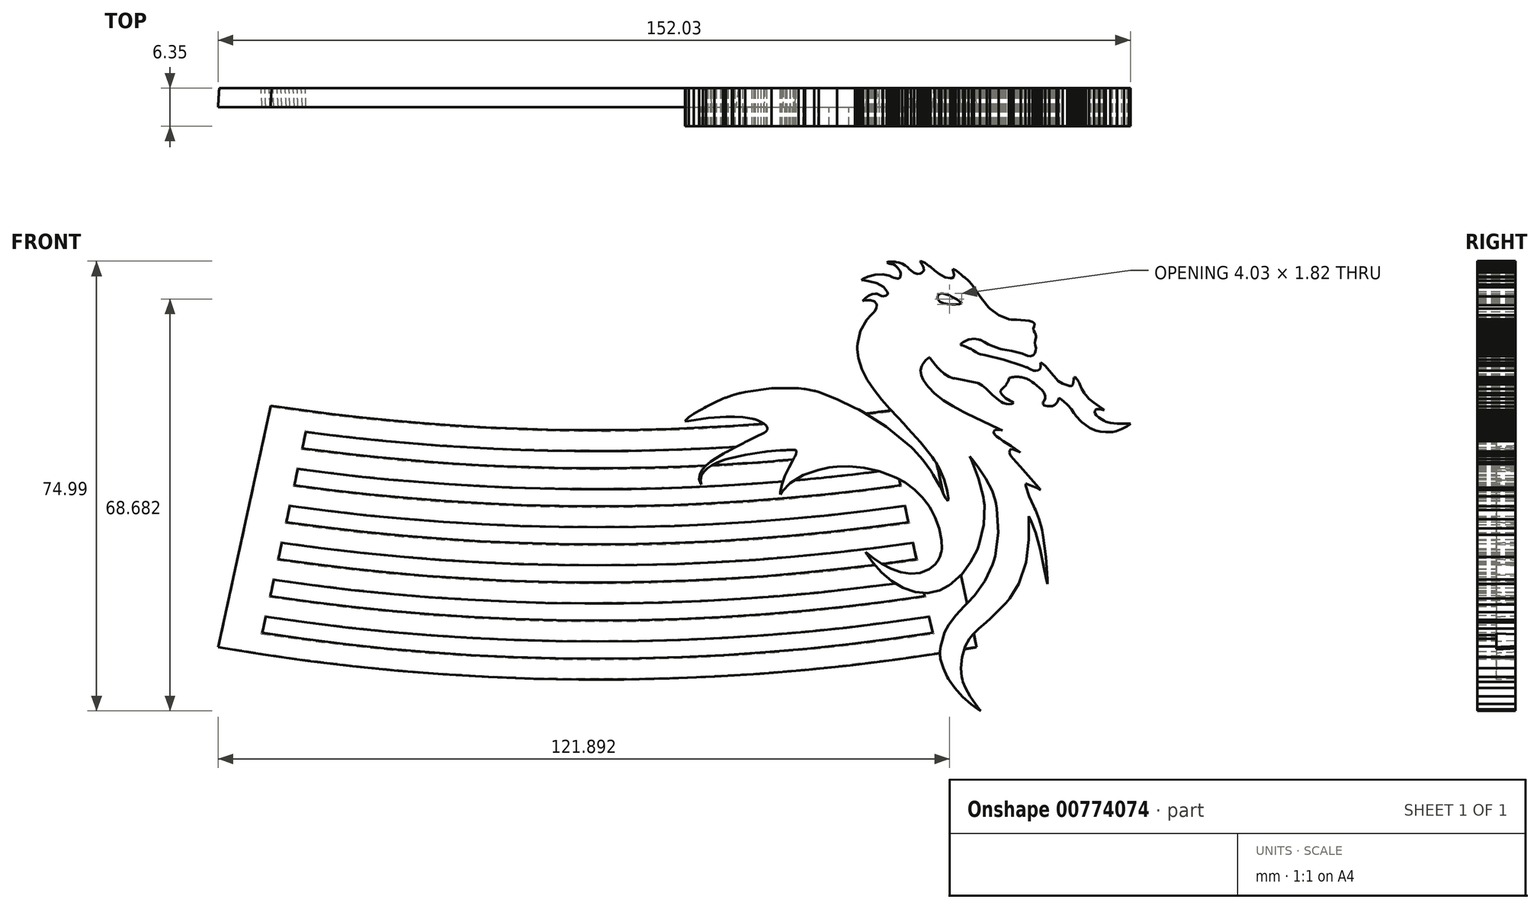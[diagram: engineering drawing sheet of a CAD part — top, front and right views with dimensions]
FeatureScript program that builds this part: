
annotation { "Feature Type Name" : "Feature", "Feature Type Description" : "" }
export const myFeature = defineFeature(function(context is Context, id is Id, definition is map)
    precondition{}
    {
        {
            var Q0;
            Q0=qCreatedBy(makeId("Front.planeOp"),FACE);
            var sketch = newSketch(context, id + "F0", { "sketchPlane" : qUnion([Q0])});
            skArc(sketch, "E0", {"start": v(-54.3, 4.59) * mm, "mid": v(0, 0.52) * mm, "end": v(54.3, 4.59) * mm});
            skArc(sketch, "E1", {"start": v(-48.68, 0.55) * mm, "mid": v(0, -2.65) * mm, "end": v(48.68, 0.55) * mm});
            skArc(sketch, "E2", {"start": v(-49.34, -2.48) * mm, "mid": v(0, -5.83) * mm, "end": v(49.34, -2.48) * mm});
            skArc(sketch, "E3", {"start": v(-50.03, -5.62) * mm, "mid": v(0, -9) * mm, "end": v(50.03, -5.62) * mm});
            skArc(sketch, "E4", {"start": v(-50.68, -8.64) * mm, "mid": v(0, -12.18) * mm, "end": v(50.68, -8.64) * mm});
            skArc(sketch, "E5", {"start": v(-51.37, -11.78) * mm, "mid": v(0, -15.35) * mm, "end": v(51.37, -11.78) * mm});
            skArc(sketch, "E6", {"start": v(-52.03, -14.8) * mm, "mid": v(0, -18.53) * mm, "end": v(52.03, -14.8) * mm});
            skArc(sketch, "E7", {"start": v(-52.71, -17.94) * mm, "mid": v(0, -21.7) * mm, "end": v(52.71, -17.94) * mm});
            skArc(sketch, "E8", {"start": v(-53.37, -20.95) * mm, "mid": v(0, -24.88) * mm, "end": v(53.37, -20.95) * mm});
            skArc(sketch, "E9", {"start": v(-54.05, -24.1) * mm, "mid": v(0, -28.05) * mm, "end": v(54.05, -24.1) * mm});
            skArc(sketch, "E10", {"start": v(-54.7, -27.1) * mm, "mid": v(0, -31.23) * mm, "end": v(54.7, -27.1) * mm});
            skArc(sketch, "E11", {"start": v(-55.4, -30.25) * mm, "mid": v(0, -34.4) * mm, "end": v(55.4, -30.25) * mm});
            skArc(sketch, "E12", {"start": v(-56.05, -33.25) * mm, "mid": v(0, -37.58) * mm, "end": v(56.05, -33.25) * mm});
            skArc(sketch, "E13", {"start": v(-63, -35.37) * mm, "mid": v(0, -40.75) * mm, "end": v(63, -35.37) * mm});
            skLineSegment(sketch, "E14", {"start": v(56.05, -33.25) * mm, "end": v(55.4, -30.25) * mm});
            skLineSegment(sketch, "E15", {"start": v(-56.05, -33.25) * mm, "end": v(-55.4, -30.25) * mm});
            skLineSegment(sketch, "E16", {"start": v(63, -35.37) * mm, "end": v(54.3, 4.59) * mm});
            skLineSegment(sketch, "E17", {"start": v(-63, -35.37) * mm, "end": v(-54.3, 4.59) * mm});
            skLineSegment(sketch, "E18.trimOffspring", {"start": v(49.34, -2.48) * mm, "end": v(48.68, 0.55) * mm});
            skLineSegment(sketch, "E19.trimOffspring", {"start": v(50.68, -8.64) * mm, "end": v(50.03, -5.62) * mm});
            skLineSegment(sketch, "E20.trimOffspring", {"start": v(52.03, -14.8) * mm, "end": v(51.37, -11.78) * mm});
            skLineSegment(sketch, "E21.trimOffspring", {"start": v(53.37, -20.95) * mm, "end": v(52.71, -17.94) * mm});
            skLineSegment(sketch, "E22.trimOffspring", {"start": v(54.7, -27.1) * mm, "end": v(54.05, -24.1) * mm});
            skLineSegment(sketch, "E23.trimOffspring", {"start": v(-49.34, -2.48) * mm, "end": v(-48.68, 0.55) * mm});
            skLineSegment(sketch, "E24.trimOffspring", {"start": v(-50.68, -8.64) * mm, "end": v(-50.03, -5.62) * mm});
            skLineSegment(sketch, "E25.trimOffspring", {"start": v(-52.03, -14.8) * mm, "end": v(-51.37, -11.78) * mm});
            skLineSegment(sketch, "E26.trimOffspring", {"start": v(-53.37, -20.95) * mm, "end": v(-52.71, -17.94) * mm});
            skLineSegment(sketch, "E27.trimOffspring", {"start": v(-54.7, -27.1) * mm, "end": v(-54.05, -24.1) * mm});
            skSolve(sketch);
        }
        {
            var Q0;
            Q0 = qSketchRegion(id + "F0", true);
            extrude(context, id + "F1", {"entities" : qUnion([Q0]), "depth" : 3.17 * mm, "offsetDistance" : 25.4 * mm, "hasDraft" : true, "draftAngle" : 3 * degree});
        }
        {
            var Q0;
            Q0=qCreatedBy(makeId("Front.planeOp"),FACE);
            var sketch = newSketch(context, id + "F2", { "sketchPlane" : qUnion([Q0])});
            skLineSegment(sketch, "E28", {"start": v(68.67, 9.41) * mm, "end": v(68.42, 8.83) * mm});
            skLineSegment(sketch, "E29", {"start": v(68.42, 8.83) * mm, "end": v(68.1, 8.27) * mm});
            skLineSegment(sketch, "E30", {"start": v(68.1, 8.27) * mm, "end": v(68.04, 8.16) * mm});
            skLineSegment(sketch, "E31", {"start": v(68.04, 8.16) * mm, "end": v(68, 8.1) * mm});
            skLineSegment(sketch, "E32", {"start": v(68, 8.1) * mm, "end": v(67.83, 7.9) * mm});
            skLineSegment(sketch, "E33", {"start": v(67.83, 7.9) * mm, "end": v(67.56, 7.67) * mm});
            skLineSegment(sketch, "E34", {"start": v(67.56, 7.67) * mm, "end": v(67.32, 7.43) * mm});
            skLineSegment(sketch, "E35", {"start": v(67.32, 7.43) * mm, "end": v(67.2, 7.21) * mm});
            skLineSegment(sketch, "E36", {"start": v(67.2, 7.21) * mm, "end": v(67.2, 7.14) * mm});
            skLineSegment(sketch, "E37", {"start": v(67.2, 7.14) * mm, "end": v(67.18, 7) * mm});
            skLineSegment(sketch, "E38", {"start": v(67.18, 7) * mm, "end": v(67.42, 6.57) * mm});
            skLineSegment(sketch, "E39", {"start": v(67.42, 6.57) * mm, "end": v(68.03, 6.05) * mm});
            skLineSegment(sketch, "E40", {"start": v(68.03, 6.05) * mm, "end": v(68.75, 5.6) * mm});
            skLineSegment(sketch, "E41", {"start": v(68.75, 5.6) * mm, "end": v(69.19, 5.37) * mm});
            skLineSegment(sketch, "E42", {"start": v(69.19, 5.37) * mm, "end": v(69.32, 5.29) * mm});
            skLineSegment(sketch, "E43", {"start": v(69.32, 5.29) * mm, "end": v(69.28, 5.21) * mm});
            skLineSegment(sketch, "E44", {"start": v(69.28, 5.21) * mm, "end": v(69.03, 5.06) * mm});
            skLineSegment(sketch, "E45", {"start": v(69.03, 5.06) * mm, "end": v(68.6, 5.02) * mm});
            skLineSegment(sketch, "E46", {"start": v(68.6, 5.02) * mm, "end": v(68.14, 5.07) * mm});
            skLineSegment(sketch, "E47", {"start": v(68.14, 5.07) * mm, "end": v(67.85, 5.14) * mm});
            skLineSegment(sketch, "E48", {"start": v(67.85, 5.14) * mm, "end": v(67.76, 5.17) * mm});
            skLineSegment(sketch, "E49", {"start": v(67.76, 5.17) * mm, "end": v(67.64, 5.2) * mm});
            skLineSegment(sketch, "E50", {"start": v(67.64, 5.2) * mm, "end": v(67.32, 5.38) * mm});
            skLineSegment(sketch, "E51", {"start": v(67.32, 5.38) * mm, "end": v(66.88, 5.7) * mm});
            skLineSegment(sketch, "E52", {"start": v(66.88, 5.7) * mm, "end": v(66.46, 6.05) * mm});
            skLineSegment(sketch, "E53", {"start": v(66.46, 6.05) * mm, "end": v(66.18, 6.3) * mm});
            skLineSegment(sketch, "E54", {"start": v(66.18, 6.3) * mm, "end": v(66.08, 6.37) * mm});
            skLineSegment(sketch, "E55", {"start": v(66.08, 6.37) * mm, "end": v(65.9, 6.5) * mm});
            skLineSegment(sketch, "E56", {"start": v(65.9, 6.5) * mm, "end": v(65.42, 6.96) * mm});
            skLineSegment(sketch, "E57", {"start": v(65.42, 6.96) * mm, "end": v(64.8, 7.59) * mm});
            skLineSegment(sketch, "E58", {"start": v(64.8, 7.59) * mm, "end": v(64.12, 8.14) * mm});
            skLineSegment(sketch, "E59", {"start": v(64.12, 8.14) * mm, "end": v(63.52, 8.48) * mm});
            skLineSegment(sketch, "E60", {"start": v(63.52, 8.48) * mm, "end": v(63.3, 8.54) * mm});
            skLineSegment(sketch, "E61", {"start": v(63.3, 8.54) * mm, "end": v(63, 8.64) * mm});
            skLineSegment(sketch, "E62", {"start": v(63, 8.64) * mm, "end": v(59.85, 9.26) * mm});
            skLineSegment(sketch, "E63", {"start": v(59.85, 9.26) * mm, "end": v(59.53, 9.3) * mm});
            skLineSegment(sketch, "E64", {"start": v(59.53, 9.3) * mm, "end": v(59.3, 9.34) * mm});
            skLineSegment(sketch, "E65", {"start": v(59.3, 9.34) * mm, "end": v(58.62, 9.58) * mm});
            skLineSegment(sketch, "E66", {"start": v(58.62, 9.58) * mm, "end": v(57.8, 10.08) * mm});
            skLineSegment(sketch, "E67", {"start": v(57.8, 10.08) * mm, "end": v(57.09, 10.72) * mm});
            skLineSegment(sketch, "E68", {"start": v(57.09, 10.72) * mm, "end": v(56.6, 11.24) * mm});
            skLineSegment(sketch, "E69", {"start": v(56.6, 11.24) * mm, "end": v(56.45, 11.42) * mm});
            skLineSegment(sketch, "E70", {"start": v(56.45, 11.42) * mm, "end": v(56.35, 11.53) * mm});
            skLineSegment(sketch, "E71", {"start": v(56.35, 11.53) * mm, "end": v(55.43, 12.69) * mm});
            skLineSegment(sketch, "E72", {"start": v(55.43, 12.69) * mm, "end": v(55.34, 12.8) * mm});
            skLineSegment(sketch, "E73", {"start": v(55.34, 12.8) * mm, "end": v(55.33, 12.82) * mm});
            skLineSegment(sketch, "E74", {"start": v(55.33, 12.82) * mm, "end": v(55.1, 12.72) * mm});
            skLineSegment(sketch, "E75", {"start": v(55.1, 12.72) * mm, "end": v(54.7, 12.3) * mm});
            skLineSegment(sketch, "E76", {"start": v(54.7, 12.3) * mm, "end": v(54.32, 11.84) * mm});
            skLineSegment(sketch, "E77", {"start": v(54.32, 11.84) * mm, "end": v(54.15, 11.6) * mm});
            skLineSegment(sketch, "E78", {"start": v(54.15, 11.6) * mm, "end": v(54.13, 11.56) * mm});
            skLineSegment(sketch, "E79", {"start": v(54.13, 11.56) * mm, "end": v(54.03, 11.35) * mm});
            skLineSegment(sketch, "E80", {"start": v(54.03, 11.35) * mm, "end": v(53.86, 10.65) * mm});
            skLineSegment(sketch, "E81", {"start": v(53.86, 10.65) * mm, "end": v(53.95, 9.83) * mm});
            skLineSegment(sketch, "E82", {"start": v(53.95, 9.83) * mm, "end": v(54.31, 9.06) * mm});
            skLineSegment(sketch, "E83", {"start": v(54.31, 9.06) * mm, "end": v(54.72, 8.46) * mm});
            skLineSegment(sketch, "E84", {"start": v(54.72, 8.46) * mm, "end": v(54.86, 8.27) * mm});
            skLineSegment(sketch, "E85", {"start": v(54.86, 8.27) * mm, "end": v(55.16, 7.88) * mm});
            skLineSegment(sketch, "E86", {"start": v(55.16, 7.88) * mm, "end": v(56.17, 6.81) * mm});
            skLineSegment(sketch, "E87", {"start": v(56.17, 6.81) * mm, "end": v(57.62, 5.65) * mm});
            skLineSegment(sketch, "E88", {"start": v(57.62, 5.65) * mm, "end": v(59.21, 4.66) * mm});
            skLineSegment(sketch, "E89", {"start": v(59.21, 4.66) * mm, "end": v(60.51, 3.98) * mm});
            skLineSegment(sketch, "E90", {"start": v(60.51, 3.98) * mm, "end": v(60.95, 3.76) * mm});
            skLineSegment(sketch, "E91", {"start": v(60.95, 3.76) * mm, "end": v(61.49, 3.49) * mm});
            skLineSegment(sketch, "E92", {"start": v(61.49, 3.49) * mm, "end": v(66.94, 0.9) * mm});
            skLineSegment(sketch, "E93", {"start": v(66.94, 0.9) * mm, "end": v(67.5, 0.66) * mm});
            skLineSegment(sketch, "E94", {"start": v(67.5, 0.66) * mm, "end": v(67.4, 0.69) * mm});
            skLineSegment(sketch, "E95", {"start": v(67.4, 0.69) * mm, "end": v(67.09, 0.75) * mm});
            skLineSegment(sketch, "E96", {"start": v(67.09, 0.75) * mm, "end": v(66.64, 0.78) * mm});
            skLineSegment(sketch, "E97", {"start": v(66.64, 0.78) * mm, "end": v(66.25, 0.68) * mm});
            skLineSegment(sketch, "E98", {"start": v(66.25, 0.68) * mm, "end": v(66.06, 0.47) * mm});
            skLineSegment(sketch, "E99", {"start": v(66.06, 0.47) * mm, "end": v(66.04, 0.39) * mm});
            skLineSegment(sketch, "E100", {"start": v(66.04, 0.39) * mm, "end": v(66.03, 0.3) * mm});
            skLineSegment(sketch, "E101", {"start": v(66.03, 0.3) * mm, "end": v(66.17, 0.01) * mm});
            skLineSegment(sketch, "E102", {"start": v(66.17, 0.01) * mm, "end": v(66.56, -0.37) * mm});
            skLineSegment(sketch, "E103", {"start": v(66.56, -0.37) * mm, "end": v(67.03, -0.71) * mm});
            skLineSegment(sketch, "E104", {"start": v(67.03, -0.71) * mm, "end": v(67.3, -0.89) * mm});
            skLineSegment(sketch, "E105", {"start": v(67.3, -0.89) * mm, "end": v(67.37, -0.94) * mm});
            skLineSegment(sketch, "E106", {"start": v(67.37, -0.94) * mm, "end": v(67.63, -1.13) * mm});
            skLineSegment(sketch, "E107", {"start": v(67.63, -1.13) * mm, "end": v(68.94, -2) * mm});
            skLineSegment(sketch, "E108", {"start": v(68.94, -2) * mm, "end": v(70.25, -2.86) * mm});
            skLineSegment(sketch, "E109", {"start": v(70.25, -2.86) * mm, "end": v(70.5, -3.05) * mm});
            skLineSegment(sketch, "E110", {"start": v(70.5, -3.05) * mm, "end": v(70.45, -3.02) * mm});
            skLineSegment(sketch, "E111", {"start": v(70.45, -3.02) * mm, "end": v(70.28, -2.94) * mm});
            skLineSegment(sketch, "E112", {"start": v(70.28, -2.94) * mm, "end": v(69.99, -2.8) * mm});
            skLineSegment(sketch, "E113", {"start": v(69.99, -2.8) * mm, "end": v(69.66, -2.66) * mm});
            skLineSegment(sketch, "E114", {"start": v(69.66, -2.66) * mm, "end": v(69.33, -2.55) * mm});
            skLineSegment(sketch, "E115", {"start": v(69.33, -2.55) * mm, "end": v(69.04, -2.5) * mm});
            skLineSegment(sketch, "E116", {"start": v(69.04, -2.5) * mm, "end": v(68.8, -2.55) * mm});
            skLineSegment(sketch, "E117", {"start": v(68.8, -2.55) * mm, "end": v(68.68, -2.74) * mm});
            skLineSegment(sketch, "E118", {"start": v(68.68, -2.74) * mm, "end": v(68.67, -3) * mm});
            skLineSegment(sketch, "E119", {"start": v(68.67, -3) * mm, "end": v(68.68, -3.09) * mm});
            skLineSegment(sketch, "E120", {"start": v(68.68, -3.09) * mm, "end": v(68.7, -3.23) * mm});
            skLineSegment(sketch, "E121", {"start": v(68.7, -3.23) * mm, "end": v(68.9, -3.62) * mm});
            skLineSegment(sketch, "E122", {"start": v(68.9, -3.62) * mm, "end": v(69.3, -4.14) * mm});
            skLineSegment(sketch, "E123", {"start": v(69.3, -4.14) * mm, "end": v(69.77, -4.64) * mm});
            skLineSegment(sketch, "E124", {"start": v(69.77, -4.64) * mm, "end": v(70.08, -4.96) * mm});
            skLineSegment(sketch, "E125", {"start": v(70.08, -4.96) * mm, "end": v(70.18, -5.08) * mm});
            skLineSegment(sketch, "E126", {"start": v(70.18, -5.08) * mm, "end": v(70.49, -5.43) * mm});
            skLineSegment(sketch, "E127", {"start": v(70.49, -5.43) * mm, "end": v(73.52, -8.92) * mm});
            skLineSegment(sketch, "E128", {"start": v(73.52, -8.92) * mm, "end": v(73.83, -9.27) * mm});
            skLineSegment(sketch, "E129", {"start": v(73.83, -9.27) * mm, "end": v(73.7, -9.2) * mm});
            skLineSegment(sketch, "E130", {"start": v(73.7, -9.2) * mm, "end": v(73.27, -8.98) * mm});
            skLineSegment(sketch, "E131", {"start": v(73.27, -8.98) * mm, "end": v(72.63, -8.69) * mm});
            skLineSegment(sketch, "E132", {"start": v(72.63, -8.69) * mm, "end": v(71.97, -8.43) * mm});
            skLineSegment(sketch, "E133", {"start": v(71.97, -8.43) * mm, "end": v(71.53, -8.29) * mm});
            skLineSegment(sketch, "E134", {"start": v(71.53, -8.29) * mm, "end": v(71.37, -8.25) * mm});
            skLineSegment(sketch, "E135", {"start": v(71.37, -8.25) * mm, "end": v(71.4, -8.6) * mm});
            skLineSegment(sketch, "E136", {"start": v(71.4, -8.6) * mm, "end": v(71.94, -10.34) * mm});
            skLineSegment(sketch, "E137", {"start": v(71.94, -10.34) * mm, "end": v(72.72, -12.01) * mm});
            skLineSegment(sketch, "E138", {"start": v(72.72, -12.01) * mm, "end": v(72.86, -12.33) * mm});
            skLineSegment(sketch, "E139", {"start": v(72.86, -12.33) * mm, "end": v(73, -12.62) * mm});
            skLineSegment(sketch, "E140", {"start": v(73, -12.62) * mm, "end": v(73.58, -14.14) * mm});
            skLineSegment(sketch, "E141", {"start": v(73.58, -14.14) * mm, "end": v(74.02, -15.71) * mm});
            skLineSegment(sketch, "E142", {"start": v(74.02, -15.71) * mm, "end": v(74.08, -16.03) * mm});
            skLineSegment(sketch, "E143", {"start": v(74.08, -16.03) * mm, "end": v(74.2, -16.77) * mm});
            skLineSegment(sketch, "E144", {"start": v(74.2, -16.77) * mm, "end": v(74.7, -20.47) * mm});
            skLineSegment(sketch, "E145", {"start": v(74.7, -20.47) * mm, "end": v(74.97, -24.2) * mm});
            skLineSegment(sketch, "E146", {"start": v(74.97, -24.2) * mm, "end": v(75, -24.95) * mm});
            skLineSegment(sketch, "E147", {"start": v(75, -24.95) * mm, "end": v(74.82, -24.23) * mm});
            skLineSegment(sketch, "E148", {"start": v(74.82, -24.23) * mm, "end": v(74.38, -22.06) * mm});
            skLineSegment(sketch, "E149", {"start": v(74.38, -22.06) * mm, "end": v(73.79, -19.2) * mm});
            skLineSegment(sketch, "E150", {"start": v(73.79, -19.2) * mm, "end": v(73.01, -16.38) * mm});
            skLineSegment(sketch, "E151", {"start": v(73.01, -16.38) * mm, "end": v(72.2, -14.31) * mm});
            skLineSegment(sketch, "E152", {"start": v(72.2, -14.31) * mm, "end": v(71.87, -13.66) * mm});
            skLineSegment(sketch, "E153", {"start": v(71.87, -13.66) * mm, "end": v(71.9, -14.63) * mm});
            skLineSegment(sketch, "E154", {"start": v(71.9, -14.63) * mm, "end": v(71.87, -17.54) * mm});
            skLineSegment(sketch, "E155", {"start": v(71.87, -17.54) * mm, "end": v(71.4, -21.31) * mm});
            skLineSegment(sketch, "E156", {"start": v(71.4, -21.31) * mm, "end": v(70.21, -24.88) * mm});
            skLineSegment(sketch, "E157", {"start": v(70.21, -24.88) * mm, "end": v(68.7, -27.4) * mm});
            skLineSegment(sketch, "E158", {"start": v(68.7, -27.4) * mm, "end": v(68.05, -28.11) * mm});
            skLineSegment(sketch, "E159", {"start": v(68.05, -28.11) * mm, "end": v(67.8, -28.38) * mm});
            skLineSegment(sketch, "E160", {"start": v(67.8, -28.38) * mm, "end": v(66.57, -29.67) * mm});
            skLineSegment(sketch, "E161", {"start": v(66.57, -29.67) * mm, "end": v(65.27, -30.9) * mm});
            skLineSegment(sketch, "E162", {"start": v(65.27, -30.9) * mm, "end": v(65, -31.15) * mm});
            skLineSegment(sketch, "E163", {"start": v(65, -31.15) * mm, "end": v(64.76, -31.36) * mm});
            skLineSegment(sketch, "E164", {"start": v(64.76, -31.36) * mm, "end": v(63.57, -32.36) * mm});
            skLineSegment(sketch, "E165", {"start": v(63.57, -32.36) * mm, "end": v(62.48, -33.46) * mm});
            skLineSegment(sketch, "E166", {"start": v(62.48, -33.46) * mm, "end": v(62.29, -33.72) * mm});
            skLineSegment(sketch, "E167", {"start": v(62.29, -33.72) * mm, "end": v(62, -34.11) * mm});
            skLineSegment(sketch, "E168", {"start": v(62, -34.11) * mm, "end": v(61.3, -35.4) * mm});
            skLineSegment(sketch, "E169", {"start": v(61.3, -35.4) * mm, "end": v(60.74, -37.16) * mm});
            skLineSegment(sketch, "E170", {"start": v(60.74, -37.16) * mm, "end": v(60.6, -39) * mm});
            skLineSegment(sketch, "E171", {"start": v(60.6, -39) * mm, "end": v(60.72, -40.45) * mm});
            skLineSegment(sketch, "E172", {"start": v(60.72, -40.45) * mm, "end": v(60.82, -40.92) * mm});
            skLineSegment(sketch, "E173", {"start": v(60.82, -40.92) * mm, "end": v(60.9, -41.28) * mm});
            skLineSegment(sketch, "E174", {"start": v(60.9, -41.28) * mm, "end": v(61.3, -42.32) * mm});
            skLineSegment(sketch, "E175", {"start": v(61.3, -42.32) * mm, "end": v(62.07, -43.66) * mm});
            skLineSegment(sketch, "E176", {"start": v(62.07, -43.66) * mm, "end": v(62.96, -44.94) * mm});
            skLineSegment(sketch, "E177", {"start": v(62.96, -44.94) * mm, "end": v(63.63, -45.83) * mm});
            skLineSegment(sketch, "E178", {"start": v(63.63, -45.83) * mm, "end": v(63.85, -46.13) * mm});
            skLineSegment(sketch, "E179", {"start": v(63.85, -46.13) * mm, "end": v(63.45, -45.87) * mm});
            skLineSegment(sketch, "E180", {"start": v(63.45, -45.87) * mm, "end": v(62.31, -45.02) * mm});
            skLineSegment(sketch, "E181", {"start": v(62.31, -45.02) * mm, "end": v(60.86, -43.74) * mm});
            skLineSegment(sketch, "E182", {"start": v(60.86, -43.74) * mm, "end": v(59.55, -42.31) * mm});
            skLineSegment(sketch, "E183", {"start": v(59.55, -42.31) * mm, "end": v(58.72, -41.17) * mm});
            skLineSegment(sketch, "E184", {"start": v(58.72, -41.17) * mm, "end": v(58.48, -40.76) * mm});
            skLineSegment(sketch, "E185", {"start": v(58.48, -40.76) * mm, "end": v(58.32, -40.48) * mm});
            skLineSegment(sketch, "E186", {"start": v(58.32, -40.48) * mm, "end": v(57.63, -39.02) * mm});
            skLineSegment(sketch, "E187", {"start": v(57.63, -39.02) * mm, "end": v(57.18, -37.47) * mm});
            skLineSegment(sketch, "E188", {"start": v(57.18, -37.47) * mm, "end": v(57.14, -37.16) * mm});
            skLineSegment(sketch, "E189", {"start": v(57.14, -37.16) * mm, "end": v(57.1, -36.92) * mm});
            skLineSegment(sketch, "E190", {"start": v(57.1, -36.92) * mm, "end": v(57.1, -36.21) * mm});
            skLineSegment(sketch, "E191", {"start": v(57.1, -36.21) * mm, "end": v(57.22, -35.3) * mm});
            skLineSegment(sketch, "E192", {"start": v(57.22, -35.3) * mm, "end": v(57.44, -34.4) * mm});
            skLineSegment(sketch, "E193", {"start": v(57.44, -34.4) * mm, "end": v(57.64, -33.71) * mm});
            skLineSegment(sketch, "E194", {"start": v(57.64, -33.71) * mm, "end": v(57.7, -33.49) * mm});
            skLineSegment(sketch, "E195", {"start": v(57.7, -33.49) * mm, "end": v(57.85, -33.03) * mm});
            skLineSegment(sketch, "E196", {"start": v(57.85, -33.03) * mm, "end": v(58.52, -31.74) * mm});
            skLineSegment(sketch, "E197", {"start": v(58.52, -31.74) * mm, "end": v(59.72, -30.17) * mm});
            skLineSegment(sketch, "E198", {"start": v(59.72, -30.17) * mm, "end": v(61.1, -28.71) * mm});
            skLineSegment(sketch, "E199", {"start": v(61.1, -28.71) * mm, "end": v(62.11, -27.67) * mm});
            skLineSegment(sketch, "E200", {"start": v(62.11, -27.67) * mm, "end": v(62.44, -27.31) * mm});
            skLineSegment(sketch, "E201", {"start": v(62.44, -27.31) * mm, "end": v(62.84, -26.87) * mm});
            skLineSegment(sketch, "E202", {"start": v(62.84, -26.87) * mm, "end": v(64.59, -24.42) * mm});
            skLineSegment(sketch, "E203", {"start": v(64.59, -24.42) * mm, "end": v(65.87, -21.72) * mm});
            skLineSegment(sketch, "E204", {"start": v(65.87, -21.72) * mm, "end": v(66.05, -21.15) * mm});
            skLineSegment(sketch, "E205", {"start": v(66.05, -21.15) * mm, "end": v(66.28, -20.35) * mm});
            skLineSegment(sketch, "E206", {"start": v(66.28, -20.35) * mm, "end": v(66.78, -16.38) * mm});
            skLineSegment(sketch, "E207", {"start": v(66.78, -16.38) * mm, "end": v(66.53, -12.38) * mm});
            skLineSegment(sketch, "E208", {"start": v(66.53, -12.38) * mm, "end": v(66.4, -11.57) * mm});
            skLineSegment(sketch, "E209", {"start": v(66.4, -11.57) * mm, "end": v(66.3, -11.02) * mm});
            skLineSegment(sketch, "E210", {"start": v(66.3, -11.02) * mm, "end": v(65.76, -9.4) * mm});
            skLineSegment(sketch, "E211", {"start": v(65.76, -9.4) * mm, "end": v(64.73, -7.37) * mm});
            skLineSegment(sketch, "E212", {"start": v(64.73, -7.37) * mm, "end": v(63.44, -5.47) * mm});
            skLineSegment(sketch, "E213", {"start": v(63.44, -5.47) * mm, "end": v(62.41, -4.14) * mm});
            skLineSegment(sketch, "E214", {"start": v(62.41, -4.14) * mm, "end": v(62.06, -3.71) * mm});
            skLineSegment(sketch, "E215", {"start": v(62.06, -3.71) * mm, "end": v(62.33, -4.33) * mm});
            skLineSegment(sketch, "E216", {"start": v(62.33, -4.33) * mm, "end": v(63.48, -7.34) * mm});
            skLineSegment(sketch, "E217", {"start": v(63.48, -7.34) * mm, "end": v(64.3, -10.46) * mm});
            skLineSegment(sketch, "E218", {"start": v(64.3, -10.46) * mm, "end": v(64.4, -11.13) * mm});
            skLineSegment(sketch, "E219", {"start": v(64.4, -11.13) * mm, "end": v(64.49, -11.79) * mm});
            skLineSegment(sketch, "E220", {"start": v(64.49, -11.79) * mm, "end": v(64.4, -15.05) * mm});
            skLineSegment(sketch, "E221", {"start": v(64.4, -15.05) * mm, "end": v(63.65, -18.22) * mm});
            skLineSegment(sketch, "E222", {"start": v(63.65, -18.22) * mm, "end": v(63.43, -18.84) * mm});
            skLineSegment(sketch, "E223", {"start": v(63.43, -18.84) * mm, "end": v(63.27, -19.27) * mm});
            skLineSegment(sketch, "E224", {"start": v(63.27, -19.27) * mm, "end": v(62.19, -21.37) * mm});
            skLineSegment(sketch, "E225", {"start": v(62.19, -21.37) * mm, "end": v(60.74, -23.3) * mm});
            skLineSegment(sketch, "E226", {"start": v(60.74, -23.3) * mm, "end": v(60.4, -23.65) * mm});
            skLineSegment(sketch, "E227", {"start": v(60.4, -23.65) * mm, "end": v(60.29, -23.76) * mm});
            skLineSegment(sketch, "E228", {"start": v(60.29, -23.76) * mm, "end": v(59.08, -24.8) * mm});
            skLineSegment(sketch, "E229", {"start": v(59.08, -24.8) * mm, "end": v(58.96, -24.89) * mm});
            skLineSegment(sketch, "E230", {"start": v(58.96, -24.89) * mm, "end": v(58.52, -25.24) * mm});
            skLineSegment(sketch, "E231", {"start": v(58.52, -25.24) * mm, "end": v(57, -26.03) * mm});
            skLineSegment(sketch, "E232", {"start": v(57, -26.03) * mm, "end": v(54.98, -26.47) * mm});
            skLineSegment(sketch, "E233", {"start": v(54.98, -26.47) * mm, "end": v(52.93, -26.29) * mm});
            skLineSegment(sketch, "E234", {"start": v(52.93, -26.29) * mm, "end": v(50.93, -25.6) * mm});
            skLineSegment(sketch, "E235", {"start": v(50.93, -25.6) * mm, "end": v(49.05, -24.48) * mm});
            skLineSegment(sketch, "E236", {"start": v(49.05, -24.48) * mm, "end": v(47.34, -23.05) * mm});
            skLineSegment(sketch, "E237", {"start": v(47.34, -23.05) * mm, "end": v(45.88, -21.39) * mm});
            skLineSegment(sketch, "E238", {"start": v(45.88, -21.39) * mm, "end": v(44.98, -20.06) * mm});
            skLineSegment(sketch, "E239", {"start": v(44.98, -20.06) * mm, "end": v(44.73, -19.6) * mm});
            skLineSegment(sketch, "E240", {"start": v(44.73, -19.6) * mm, "end": v(45.02, -19.87) * mm});
            skLineSegment(sketch, "E241", {"start": v(45.02, -19.87) * mm, "end": v(45.95, -20.63) * mm});
            skLineSegment(sketch, "E242", {"start": v(45.95, -20.63) * mm, "end": v(47.38, -21.6) * mm});
            skLineSegment(sketch, "E243", {"start": v(47.38, -21.6) * mm, "end": v(48.94, -22.42) * mm});
            skLineSegment(sketch, "E244", {"start": v(48.94, -22.42) * mm, "end": v(50.57, -23) * mm});
            skLineSegment(sketch, "E245", {"start": v(50.57, -23) * mm, "end": v(52.21, -23.26) * mm});
            skLineSegment(sketch, "E246", {"start": v(52.21, -23.26) * mm, "end": v(53.8, -23.12) * mm});
            skLineSegment(sketch, "E247", {"start": v(53.8, -23.12) * mm, "end": v(55.28, -22.5) * mm});
            skLineSegment(sketch, "E248", {"start": v(55.28, -22.5) * mm, "end": v(56.31, -21.65) * mm});
            skLineSegment(sketch, "E249", {"start": v(56.31, -21.65) * mm, "end": v(56.58, -21.3) * mm});
            skLineSegment(sketch, "E250", {"start": v(56.58, -21.3) * mm, "end": v(56.68, -21.16) * mm});
            skLineSegment(sketch, "E251", {"start": v(56.68, -21.16) * mm, "end": v(57.06, -20.4) * mm});
            skLineSegment(sketch, "E252", {"start": v(57.06, -20.4) * mm, "end": v(57.3, -19.67) * mm});
            skLineSegment(sketch, "E253", {"start": v(57.3, -19.67) * mm, "end": v(57.31, -19.54) * mm});
            skLineSegment(sketch, "E254", {"start": v(57.31, -19.54) * mm, "end": v(57.38, -19.07) * mm});
            skLineSegment(sketch, "E255", {"start": v(57.38, -19.07) * mm, "end": v(57.34, -17.64) * mm});
            skLineSegment(sketch, "E256", {"start": v(57.34, -17.64) * mm, "end": v(56.95, -15.7) * mm});
            skLineSegment(sketch, "E257", {"start": v(56.95, -15.7) * mm, "end": v(56.25, -13.83) * mm});
            skLineSegment(sketch, "E258", {"start": v(56.25, -13.83) * mm, "end": v(55.6, -12.56) * mm});
            skLineSegment(sketch, "E259", {"start": v(55.6, -12.56) * mm, "end": v(55.35, -12.15) * mm});
            skLineSegment(sketch, "E260", {"start": v(55.35, -12.15) * mm, "end": v(55.09, -11.74) * mm});
            skLineSegment(sketch, "E261", {"start": v(55.09, -11.74) * mm, "end": v(54.2, -10.58) * mm});
            skLineSegment(sketch, "E262", {"start": v(54.2, -10.58) * mm, "end": v(52.8, -9.19) * mm});
            skLineSegment(sketch, "E263", {"start": v(52.8, -9.19) * mm, "end": v(51.22, -8.02) * mm});
            skLineSegment(sketch, "E264", {"start": v(51.22, -8.02) * mm, "end": v(49.92, -7.3) * mm});
            skLineSegment(sketch, "E265", {"start": v(49.92, -7.3) * mm, "end": v(49.47, -7.11) * mm});
            skLineSegment(sketch, "E266", {"start": v(49.47, -7.11) * mm, "end": v(48.85, -6.85) * mm});
            skLineSegment(sketch, "E267", {"start": v(48.85, -6.85) * mm, "end": v(46.96, -6.19) * mm});
            skLineSegment(sketch, "E268", {"start": v(46.96, -6.19) * mm, "end": v(44.46, -5.59) * mm});
            skLineSegment(sketch, "E269", {"start": v(44.46, -5.59) * mm, "end": v(41.92, -5.34) * mm});
            skLineSegment(sketch, "E270", {"start": v(41.92, -5.34) * mm, "end": v(39.9, -5.4) * mm});
            skLineSegment(sketch, "E271", {"start": v(39.9, -5.4) * mm, "end": v(39.24, -5.47) * mm});
            skLineSegment(sketch, "E272", {"start": v(39.24, -5.47) * mm, "end": v(38.61, -5.55) * mm});
            skLineSegment(sketch, "E273", {"start": v(38.61, -5.55) * mm, "end": v(36.74, -5.94) * mm});
            skLineSegment(sketch, "E274", {"start": v(36.74, -5.94) * mm, "end": v(34.31, -6.81) * mm});
            skLineSegment(sketch, "E275", {"start": v(34.31, -6.81) * mm, "end": v(32.16, -8.15) * mm});
            skLineSegment(sketch, "E276", {"start": v(32.16, -8.15) * mm, "end": v(30.8, -9.52) * mm});
            skLineSegment(sketch, "E277", {"start": v(30.8, -9.52) * mm, "end": v(30.46, -10.05) * mm});
            skLineSegment(sketch, "E278", {"start": v(30.46, -10.05) * mm, "end": v(30.48, -9.64) * mm});
            skLineSegment(sketch, "E279", {"start": v(30.48, -9.64) * mm, "end": v(30.73, -8.42) * mm});
            skLineSegment(sketch, "E280", {"start": v(30.73, -8.42) * mm, "end": v(31.26, -6.95) * mm});
            skLineSegment(sketch, "E281", {"start": v(31.26, -6.95) * mm, "end": v(31.96, -5.52) * mm});
            skLineSegment(sketch, "E282", {"start": v(31.96, -5.52) * mm, "end": v(32.52, -4.42) * mm});
            skLineSegment(sketch, "E283", {"start": v(32.52, -4.42) * mm, "end": v(32.7, -4.05) * mm});
            skLineSegment(sketch, "E284", {"start": v(32.7, -4.05) * mm, "end": v(32.74, -3.97) * mm});
            skLineSegment(sketch, "E285", {"start": v(32.74, -3.97) * mm, "end": v(32.87, -3.74) * mm});
            skLineSegment(sketch, "E286", {"start": v(32.87, -3.74) * mm, "end": v(33.06, -3.35) * mm});
            skLineSegment(sketch, "E287", {"start": v(33.06, -3.35) * mm, "end": v(33.17, -2.96) * mm});
            skLineSegment(sketch, "E288", {"start": v(33.17, -2.96) * mm, "end": v(33.12, -2.71) * mm});
            skLineSegment(sketch, "E289", {"start": v(33.12, -2.71) * mm, "end": v(33.07, -2.67) * mm});
            skLineSegment(sketch, "E290", {"start": v(33.07, -2.67) * mm, "end": v(33.01, -2.62) * mm});
            skLineSegment(sketch, "E291", {"start": v(33.01, -2.62) * mm, "end": v(32.74, -2.59) * mm});
            skLineSegment(sketch, "E292", {"start": v(32.74, -2.59) * mm, "end": v(32.2, -2.59) * mm});
            skLineSegment(sketch, "E293", {"start": v(32.2, -2.59) * mm, "end": v(31.65, -2.62) * mm});
            skLineSegment(sketch, "E294", {"start": v(31.65, -2.62) * mm, "end": v(31.38, -2.64) * mm});
            skLineSegment(sketch, "E295", {"start": v(31.38, -2.64) * mm, "end": v(31.3, -2.64) * mm});
            skLineSegment(sketch, "E296", {"start": v(31.3, -2.64) * mm, "end": v(30.46, -2.64) * mm});
            skLineSegment(sketch, "E297", {"start": v(30.46, -2.64) * mm, "end": v(28.22, -2.87) * mm});
            skLineSegment(sketch, "E298", {"start": v(28.22, -2.87) * mm, "end": v(27.95, -2.92) * mm});
            skLineSegment(sketch, "E299", {"start": v(27.95, -2.92) * mm, "end": v(27.4, -3) * mm});
            skLineSegment(sketch, "E300", {"start": v(27.4, -3) * mm, "end": v(24.6, -3.45) * mm});
            skLineSegment(sketch, "E301", {"start": v(24.6, -3.45) * mm, "end": v(21.86, -4.04) * mm});
            skLineSegment(sketch, "E302", {"start": v(21.86, -4.04) * mm, "end": v(21.32, -4.2) * mm});
            skLineSegment(sketch, "E303", {"start": v(21.32, -4.2) * mm, "end": v(21.15, -4.26) * mm});
            skLineSegment(sketch, "E304", {"start": v(21.15, -4.26) * mm, "end": v(20.64, -4.44) * mm});
            skLineSegment(sketch, "E305", {"start": v(20.64, -4.44) * mm, "end": v(19.87, -4.75) * mm});
            skLineSegment(sketch, "E306", {"start": v(19.87, -4.75) * mm, "end": v(19.1, -5.15) * mm});
            skLineSegment(sketch, "E307", {"start": v(19.1, -5.15) * mm, "end": v(18.37, -5.63) * mm});
            skLineSegment(sketch, "E308", {"start": v(18.37, -5.63) * mm, "end": v(17.77, -6.2) * mm});
            skLineSegment(sketch, "E309", {"start": v(17.77, -6.2) * mm, "end": v(17.35, -6.84) * mm});
            skLineSegment(sketch, "E310", {"start": v(17.35, -6.84) * mm, "end": v(17.18, -7.56) * mm});
            skLineSegment(sketch, "E311", {"start": v(17.18, -7.56) * mm, "end": v(17.26, -8.18) * mm});
            skLineSegment(sketch, "E312", {"start": v(17.26, -8.18) * mm, "end": v(17.33, -8.37) * mm});
            skLineSegment(sketch, "E313", {"start": v(17.33, -8.37) * mm, "end": v(17.2, -8.18) * mm});
            skLineSegment(sketch, "E314", {"start": v(17.2, -8.18) * mm, "end": v(16.98, -7.5) * mm});
            skLineSegment(sketch, "E315", {"start": v(16.98, -7.5) * mm, "end": v(17.05, -6.67) * mm});
            skLineSegment(sketch, "E316", {"start": v(17.05, -6.67) * mm, "end": v(17.45, -5.9) * mm});
            skLineSegment(sketch, "E317", {"start": v(17.45, -5.9) * mm, "end": v(18.08, -5.2) * mm});
            skLineSegment(sketch, "E318", {"start": v(18.08, -5.2) * mm, "end": v(18.87, -4.56) * mm});
            skLineSegment(sketch, "E319", {"start": v(18.87, -4.56) * mm, "end": v(19.73, -3.99) * mm});
            skLineSegment(sketch, "E320", {"start": v(19.73, -3.99) * mm, "end": v(20.56, -3.49) * mm});
            skLineSegment(sketch, "E321", {"start": v(20.56, -3.49) * mm, "end": v(21.1, -3.17) * mm});
            skLineSegment(sketch, "E322", {"start": v(21.1, -3.17) * mm, "end": v(21.29, -3.07) * mm});
            skLineSegment(sketch, "E323", {"start": v(21.29, -3.07) * mm, "end": v(21.56, -2.9) * mm});
            skLineSegment(sketch, "E324", {"start": v(21.56, -2.9) * mm, "end": v(22.96, -2.17) * mm});
            skLineSegment(sketch, "E325", {"start": v(22.96, -2.17) * mm, "end": v(24.37, -1.45) * mm});
            skLineSegment(sketch, "E326", {"start": v(24.37, -1.45) * mm, "end": v(24.65, -1.3) * mm});
            skLineSegment(sketch, "E327", {"start": v(24.65, -1.3) * mm, "end": v(24.92, -1.15) * mm});
            skLineSegment(sketch, "E328", {"start": v(24.92, -1.15) * mm, "end": v(26.37, -0.48) * mm});
            skLineSegment(sketch, "E329", {"start": v(26.37, -0.48) * mm, "end": v(27.78, 0.25) * mm});
            skLineSegment(sketch, "E330", {"start": v(27.78, 0.25) * mm, "end": v(28.03, 0.43) * mm});
            skLineSegment(sketch, "E331", {"start": v(28.03, 0.43) * mm, "end": v(28.12, 0.49) * mm});
            skLineSegment(sketch, "E332", {"start": v(28.12, 0.49) * mm, "end": v(28.33, 0.76) * mm});
            skLineSegment(sketch, "E333", {"start": v(28.33, 0.76) * mm, "end": v(28.33, 1.1) * mm});
            skLineSegment(sketch, "E334", {"start": v(28.33, 1.1) * mm, "end": v(28.11, 1.44) * mm});
            skLineSegment(sketch, "E335", {"start": v(28.11, 1.44) * mm, "end": v(27.74, 1.75) * mm});
            skLineSegment(sketch, "E336", {"start": v(27.74, 1.75) * mm, "end": v(27.27, 2.03) * mm});
            skLineSegment(sketch, "E337", {"start": v(27.27, 2.03) * mm, "end": v(26.79, 2.27) * mm});
            skLineSegment(sketch, "E338", {"start": v(26.79, 2.27) * mm, "end": v(26.35, 2.45) * mm});
            skLineSegment(sketch, "E339", {"start": v(26.35, 2.45) * mm, "end": v(26.12, 2.53) * mm});
            skLineSegment(sketch, "E340", {"start": v(26.12, 2.53) * mm, "end": v(26.04, 2.55) * mm});
            skLineSegment(sketch, "E341", {"start": v(26.04, 2.55) * mm, "end": v(25.75, 2.63) * mm});
            skLineSegment(sketch, "E342", {"start": v(25.75, 2.63) * mm, "end": v(24.24, 2.86) * mm});
            skLineSegment(sketch, "E343", {"start": v(24.24, 2.86) * mm, "end": v(22.87, 2.94) * mm});
            skLineSegment(sketch, "E344", {"start": v(22.87, 2.94) * mm, "end": v(22.42, 2.94) * mm});
            skLineSegment(sketch, "E345", {"start": v(22.42, 2.94) * mm, "end": v(21.44, 2.94) * mm});
            skLineSegment(sketch, "E346", {"start": v(21.44, 2.94) * mm, "end": v(18.5, 2.7) * mm});
            skLineSegment(sketch, "E347", {"start": v(18.5, 2.7) * mm, "end": v(15.25, 2.25) * mm});
            skLineSegment(sketch, "E348", {"start": v(15.25, 2.25) * mm, "end": v(14.61, 2.13) * mm});
            skLineSegment(sketch, "E349", {"start": v(14.61, 2.13) * mm, "end": v(14.73, 2.33) * mm});
            skLineSegment(sketch, "E350", {"start": v(14.73, 2.33) * mm, "end": v(15.23, 2.83) * mm});
            skLineSegment(sketch, "E351", {"start": v(15.23, 2.83) * mm, "end": v(16.06, 3.42) * mm});
            skLineSegment(sketch, "E352", {"start": v(16.06, 3.42) * mm, "end": v(16.97, 3.94) * mm});
            skLineSegment(sketch, "E353", {"start": v(16.97, 3.94) * mm, "end": v(17.6, 4.27) * mm});
            skLineSegment(sketch, "E354", {"start": v(17.6, 4.27) * mm, "end": v(17.8, 4.39) * mm});
            skLineSegment(sketch, "E355", {"start": v(17.8, 4.39) * mm, "end": v(18.09, 4.55) * mm});
            skLineSegment(sketch, "E356", {"start": v(18.09, 4.55) * mm, "end": v(19.5, 5.3) * mm});
            skLineSegment(sketch, "E357", {"start": v(19.5, 5.3) * mm, "end": v(20.96, 5.94) * mm});
            skLineSegment(sketch, "E358", {"start": v(20.96, 5.94) * mm, "end": v(21.27, 6.06) * mm});
            skLineSegment(sketch, "E359", {"start": v(21.27, 6.06) * mm, "end": v(21.37, 6.1) * mm});
            skLineSegment(sketch, "E360", {"start": v(21.37, 6.1) * mm, "end": v(22.41, 6.47) * mm});
            skLineSegment(sketch, "E361", {"start": v(22.41, 6.47) * mm, "end": v(22.52, 6.5) * mm});
            skLineSegment(sketch, "E362", {"start": v(22.52, 6.5) * mm, "end": v(22.63, 6.54) * mm});
            skLineSegment(sketch, "E363", {"start": v(22.63, 6.54) * mm, "end": v(23.7, 6.83) * mm});
            skLineSegment(sketch, "E364", {"start": v(23.7, 6.83) * mm, "end": v(23.8, 6.85) * mm});
            skLineSegment(sketch, "E365", {"start": v(23.8, 6.85) * mm, "end": v(24.65, 7.05) * mm});
            skLineSegment(sketch, "E366", {"start": v(24.65, 7.05) * mm, "end": v(29.04, 7.67) * mm});
            skLineSegment(sketch, "E367", {"start": v(29.04, 7.67) * mm, "end": v(33.52, 7.66) * mm});
            skLineSegment(sketch, "E368", {"start": v(33.52, 7.66) * mm, "end": v(34.42, 7.54) * mm});
            skLineSegment(sketch, "E369", {"start": v(34.42, 7.54) * mm, "end": v(34.57, 7.53) * mm});
            skLineSegment(sketch, "E370", {"start": v(34.57, 7.53) * mm, "end": v(36.1, 7.26) * mm});
            skLineSegment(sketch, "E371", {"start": v(36.1, 7.26) * mm, "end": v(36.25, 7.21) * mm});
            skLineSegment(sketch, "E372", {"start": v(36.25, 7.21) * mm, "end": v(36.88, 7.01) * mm});
            skLineSegment(sketch, "E373", {"start": v(36.88, 7.01) * mm, "end": v(39.96, 5.82) * mm});
            skLineSegment(sketch, "E374", {"start": v(39.96, 5.82) * mm, "end": v(42.95, 4.4) * mm});
            skLineSegment(sketch, "E375", {"start": v(42.95, 4.4) * mm, "end": v(43.54, 4.1) * mm});
            skLineSegment(sketch, "E376", {"start": v(43.54, 4.1) * mm, "end": v(44.34, 3.68) * mm});
            skLineSegment(sketch, "E377", {"start": v(44.34, 3.68) * mm, "end": v(48.14, 1.25) * mm});
            skLineSegment(sketch, "E378", {"start": v(48.14, 1.25) * mm, "end": v(51.64, -1.58) * mm});
            skLineSegment(sketch, "E379", {"start": v(51.64, -1.58) * mm, "end": v(52.3, -2.2) * mm});
            skLineSegment(sketch, "E380", {"start": v(52.3, -2.2) * mm, "end": v(52.64, -2.51) * mm});
            skLineSegment(sketch, "E381", {"start": v(52.64, -2.51) * mm, "end": v(54.23, -4.24) * mm});
            skLineSegment(sketch, "E382", {"start": v(54.23, -4.24) * mm, "end": v(55.6, -6.14) * mm});
            skLineSegment(sketch, "E383", {"start": v(55.6, -6.14) * mm, "end": v(55.84, -6.55) * mm});
            skLineSegment(sketch, "E384", {"start": v(55.84, -6.55) * mm, "end": v(55.95, -6.74) * mm});
            skLineSegment(sketch, "E385", {"start": v(55.95, -6.74) * mm, "end": v(57.1, -8.7) * mm});
            skLineSegment(sketch, "E386", {"start": v(57.1, -8.7) * mm, "end": v(57.22, -8.9) * mm});
            skLineSegment(sketch, "E387", {"start": v(57.22, -8.9) * mm, "end": v(57.29, -9.04) * mm});
            skLineSegment(sketch, "E388", {"start": v(57.29, -9.04) * mm, "end": v(57.48, -9.46) * mm});
            skLineSegment(sketch, "E389", {"start": v(57.48, -9.46) * mm, "end": v(57.74, -10.08) * mm});
            skLineSegment(sketch, "E390", {"start": v(57.74, -10.08) * mm, "end": v(58.05, -10.66) * mm});
            skLineSegment(sketch, "E391", {"start": v(58.05, -10.66) * mm, "end": v(58.33, -11.03) * mm});
            skLineSegment(sketch, "E392", {"start": v(58.33, -11.03) * mm, "end": v(58.44, -11.12) * mm});
            skLineSegment(sketch, "E393", {"start": v(58.44, -11.12) * mm, "end": v(58.45, -10.69) * mm});
            skLineSegment(sketch, "E394", {"start": v(58.45, -10.69) * mm, "end": v(58.28, -9.4) * mm});
            skLineSegment(sketch, "E395", {"start": v(58.28, -9.4) * mm, "end": v(57.78, -7.57) * mm});
            skLineSegment(sketch, "E396", {"start": v(57.78, -7.57) * mm, "end": v(57.04, -5.81) * mm});
            skLineSegment(sketch, "E397", {"start": v(57.04, -5.81) * mm, "end": v(56.4, -4.66) * mm});
            skLineSegment(sketch, "E398", {"start": v(56.4, -4.66) * mm, "end": v(56.16, -4.3) * mm});
            skLineSegment(sketch, "E399", {"start": v(56.16, -4.3) * mm, "end": v(55.79, -3.78) * mm});
            skLineSegment(sketch, "E400", {"start": v(55.79, -3.78) * mm, "end": v(53.84, -1.37) * mm});
            skLineSegment(sketch, "E401", {"start": v(53.84, -1.37) * mm, "end": v(51.76, 0.95) * mm});
            skLineSegment(sketch, "E402", {"start": v(51.76, 0.95) * mm, "end": v(51.34, 1.42) * mm});
            skLineSegment(sketch, "E403", {"start": v(51.34, 1.42) * mm, "end": v(51.03, 1.77) * mm});
            skLineSegment(sketch, "E404", {"start": v(51.03, 1.77) * mm, "end": v(50.07, 2.8) * mm});
            skLineSegment(sketch, "E405", {"start": v(50.07, 2.8) * mm, "end": v(48.71, 4.27) * mm});
            skLineSegment(sketch, "E406", {"start": v(48.71, 4.27) * mm, "end": v(47.36, 5.8) * mm});
            skLineSegment(sketch, "E407", {"start": v(47.36, 5.8) * mm, "end": v(46.08, 7.41) * mm});
            skLineSegment(sketch, "E408", {"start": v(46.08, 7.41) * mm, "end": v(44.96, 9.1) * mm});
            skLineSegment(sketch, "E409", {"start": v(44.96, 9.1) * mm, "end": v(44.07, 10.87) * mm});
            skLineSegment(sketch, "E410", {"start": v(44.07, 10.87) * mm, "end": v(43.5, 12.71) * mm});
            skLineSegment(sketch, "E411", {"start": v(43.5, 12.71) * mm, "end": v(43.31, 14.16) * mm});
            skLineSegment(sketch, "E412", {"start": v(43.31, 14.16) * mm, "end": v(43.32, 14.65) * mm});
            skLineSegment(sketch, "E413", {"start": v(43.32, 14.65) * mm, "end": v(43.33, 15.1) * mm});
            skLineSegment(sketch, "E414", {"start": v(43.33, 15.1) * mm, "end": v(43.83, 17.21) * mm});
            skLineSegment(sketch, "E415", {"start": v(43.83, 17.21) * mm, "end": v(44.9, 19.1) * mm});
            skLineSegment(sketch, "E416", {"start": v(44.9, 19.1) * mm, "end": v(45.2, 19.45) * mm});
            skLineSegment(sketch, "E417", {"start": v(45.2, 19.45) * mm, "end": v(45.3, 19.57) * mm});
            skLineSegment(sketch, "E418", {"start": v(45.3, 19.57) * mm, "end": v(45.66, 19.93) * mm});
            skLineSegment(sketch, "E419", {"start": v(45.66, 19.93) * mm, "end": v(46.14, 20.45) * mm});
            skLineSegment(sketch, "E420", {"start": v(46.14, 20.45) * mm, "end": v(46.48, 21.02) * mm});
            skLineSegment(sketch, "E421", {"start": v(46.48, 21.02) * mm, "end": v(46.55, 21.5) * mm});
            skLineSegment(sketch, "E422", {"start": v(46.55, 21.5) * mm, "end": v(46.51, 21.66) * mm});
            skLineSegment(sketch, "E423", {"start": v(46.51, 21.66) * mm, "end": v(46.48, 21.8) * mm});
            skLineSegment(sketch, "E424", {"start": v(46.48, 21.8) * mm, "end": v(46.14, 22.16) * mm});
            skLineSegment(sketch, "E425", {"start": v(46.14, 22.16) * mm, "end": v(45.5, 22.36) * mm});
            skLineSegment(sketch, "E426", {"start": v(45.5, 22.36) * mm, "end": v(44.78, 22.35) * mm});
            skLineSegment(sketch, "E427", {"start": v(44.78, 22.35) * mm, "end": v(44.32, 22.26) * mm});
            skLineSegment(sketch, "E428", {"start": v(44.32, 22.26) * mm, "end": v(44.18, 22.21) * mm});
            skLineSegment(sketch, "E429", {"start": v(44.18, 22.21) * mm, "end": v(44.3, 22.35) * mm});
            skLineSegment(sketch, "E430", {"start": v(44.3, 22.35) * mm, "end": v(44.68, 22.76) * mm});
            skLineSegment(sketch, "E431", {"start": v(44.68, 22.76) * mm, "end": v(45.18, 23.12) * mm});
            skLineSegment(sketch, "E432", {"start": v(45.18, 23.12) * mm, "end": v(45.75, 23.35) * mm});
            skLineSegment(sketch, "E433", {"start": v(45.75, 23.35) * mm, "end": v(46.3, 23.44) * mm});
            skLineSegment(sketch, "E434", {"start": v(46.3, 23.44) * mm, "end": v(46.48, 23.45) * mm});
            skLineSegment(sketch, "E435", {"start": v(46.48, 23.45) * mm, "end": v(46.58, 23.46) * mm});
            skLineSegment(sketch, "E436", {"start": v(46.58, 23.46) * mm, "end": v(47, 23.26) * mm});
            skLineSegment(sketch, "E437", {"start": v(47, 23.26) * mm, "end": v(47.4, 23.03) * mm});
            skLineSegment(sketch, "E438", {"start": v(47.4, 23.03) * mm, "end": v(47.48, 23.02) * mm});
            skLineSegment(sketch, "E439", {"start": v(47.48, 23.02) * mm, "end": v(47.54, 23.01) * mm});
            skLineSegment(sketch, "E440", {"start": v(47.54, 23.01) * mm, "end": v(47.74, 23.04) * mm});
            skLineSegment(sketch, "E441", {"start": v(47.74, 23.04) * mm, "end": v(48.05, 23.13) * mm});
            skLineSegment(sketch, "E442", {"start": v(48.05, 23.13) * mm, "end": v(48.29, 23.3) * mm});
            skLineSegment(sketch, "E443", {"start": v(48.29, 23.3) * mm, "end": v(48.36, 23.5) * mm});
            skLineSegment(sketch, "E444", {"start": v(48.36, 23.5) * mm, "end": v(48.35, 23.55) * mm});
            skLineSegment(sketch, "E445", {"start": v(48.35, 23.55) * mm, "end": v(48.29, 23.83) * mm});
            skLineSegment(sketch, "E446", {"start": v(48.29, 23.83) * mm, "end": v(47.7, 24.57) * mm});
            skLineSegment(sketch, "E447", {"start": v(47.7, 24.57) * mm, "end": v(46.53, 25.2) * mm});
            skLineSegment(sketch, "E448", {"start": v(46.53, 25.2) * mm, "end": v(45.18, 25.55) * mm});
            skLineSegment(sketch, "E449", {"start": v(45.18, 25.55) * mm, "end": v(44.28, 25.68) * mm});
            skLineSegment(sketch, "E450", {"start": v(44.28, 25.68) * mm, "end": v(43.97, 25.71) * mm});
            skLineSegment(sketch, "E451", {"start": v(43.97, 25.71) * mm, "end": v(44.23, 25.88) * mm});
            skLineSegment(sketch, "E452", {"start": v(44.23, 25.88) * mm, "end": v(45.06, 26.26) * mm});
            skLineSegment(sketch, "E453", {"start": v(45.06, 26.26) * mm, "end": v(46.3, 26.58) * mm});
            skLineSegment(sketch, "E454", {"start": v(46.3, 26.58) * mm, "end": v(47.58, 26.64) * mm});
            skLineSegment(sketch, "E455", {"start": v(47.58, 26.64) * mm, "end": v(48.49, 26.49) * mm});
            skLineSegment(sketch, "E456", {"start": v(48.49, 26.49) * mm, "end": v(48.77, 26.38) * mm});
            skLineSegment(sketch, "E457", {"start": v(48.77, 26.38) * mm, "end": v(48.85, 26.35) * mm});
            skLineSegment(sketch, "E458", {"start": v(48.85, 26.35) * mm, "end": v(49.1, 26.25) * mm});
            skLineSegment(sketch, "E459", {"start": v(49.1, 26.25) * mm, "end": v(49.42, 26.11) * mm});
            skLineSegment(sketch, "E460", {"start": v(49.42, 26.11) * mm, "end": v(49.72, 26) * mm});
            skLineSegment(sketch, "E461", {"start": v(49.72, 26) * mm, "end": v(50, 25.95) * mm});
            skLineSegment(sketch, "E462", {"start": v(50, 25.95) * mm, "end": v(50.22, 25.97) * mm});
            skLineSegment(sketch, "E463", {"start": v(50.22, 25.97) * mm, "end": v(50.4, 26.1) * mm});
            skLineSegment(sketch, "E464", {"start": v(50.4, 26.1) * mm, "end": v(50.5, 26.34) * mm});
            skLineSegment(sketch, "E465", {"start": v(50.5, 26.34) * mm, "end": v(50.54, 26.64) * mm});
            skLineSegment(sketch, "E466", {"start": v(50.54, 26.64) * mm, "end": v(50.54, 26.74) * mm});
            skLineSegment(sketch, "E467", {"start": v(50.54, 26.74) * mm, "end": v(50.54, 26.86) * mm});
            skLineSegment(sketch, "E468", {"start": v(50.54, 26.86) * mm, "end": v(50.4, 27.22) * mm});
            skLineSegment(sketch, "E469", {"start": v(50.4, 27.22) * mm, "end": v(50.05, 27.74) * mm});
            skLineSegment(sketch, "E470", {"start": v(50.05, 27.74) * mm, "end": v(49.59, 28.18) * mm});
            skLineSegment(sketch, "E471", {"start": v(49.59, 28.18) * mm, "end": v(49.25, 28.37) * mm});
            skLineSegment(sketch, "E472", {"start": v(49.25, 28.37) * mm, "end": v(49.13, 28.38) * mm});
            skLineSegment(sketch, "E473", {"start": v(49.13, 28.38) * mm, "end": v(49.1, 28.39) * mm});
            skLineSegment(sketch, "E474", {"start": v(49.1, 28.39) * mm, "end": v(48.95, 28.41) * mm});
            skLineSegment(sketch, "E475", {"start": v(48.95, 28.41) * mm, "end": v(48.65, 28.47) * mm});
            skLineSegment(sketch, "E476", {"start": v(48.65, 28.47) * mm, "end": v(48.38, 28.56) * mm});
            skLineSegment(sketch, "E477", {"start": v(48.38, 28.56) * mm, "end": v(48.28, 28.65) * mm});
            skLineSegment(sketch, "E478", {"start": v(48.28, 28.65) * mm, "end": v(48.29, 28.66) * mm});
            skLineSegment(sketch, "E479", {"start": v(48.29, 28.66) * mm, "end": v(48.3, 28.7) * mm});
            skLineSegment(sketch, "E480", {"start": v(48.3, 28.7) * mm, "end": v(48.5, 28.75) * mm});
            skLineSegment(sketch, "E481", {"start": v(48.5, 28.75) * mm, "end": v(48.9, 28.77) * mm});
            skLineSegment(sketch, "E482", {"start": v(48.9, 28.77) * mm, "end": v(49.32, 28.76) * mm});
            skLineSegment(sketch, "E483", {"start": v(49.32, 28.76) * mm, "end": v(49.56, 28.74) * mm});
            skLineSegment(sketch, "E484", {"start": v(49.56, 28.74) * mm, "end": v(49.61, 28.73) * mm});
            skLineSegment(sketch, "E485", {"start": v(49.61, 28.73) * mm, "end": v(49.77, 28.72) * mm});
            skLineSegment(sketch, "E486", {"start": v(49.77, 28.72) * mm, "end": v(50.24, 28.62) * mm});
            skLineSegment(sketch, "E487", {"start": v(50.24, 28.62) * mm, "end": v(50.78, 28.42) * mm});
            skLineSegment(sketch, "E488", {"start": v(50.78, 28.42) * mm, "end": v(51.29, 28.13) * mm});
            skLineSegment(sketch, "E489", {"start": v(51.29, 28.13) * mm, "end": v(51.67, 27.84) * mm});
            skLineSegment(sketch, "E490", {"start": v(51.67, 27.84) * mm, "end": v(51.79, 27.74) * mm});
            skLineSegment(sketch, "E491", {"start": v(51.79, 27.74) * mm, "end": v(51.9, 27.63) * mm});
            skLineSegment(sketch, "E492", {"start": v(51.9, 27.63) * mm, "end": v(52.25, 27.33) * mm});
            skLineSegment(sketch, "E493", {"start": v(52.25, 27.33) * mm, "end": v(52.76, 26.95) * mm});
            skLineSegment(sketch, "E494", {"start": v(52.76, 26.95) * mm, "end": v(53.33, 26.75) * mm});
            skLineSegment(sketch, "E495", {"start": v(53.33, 26.75) * mm, "end": v(53.8, 26.8) * mm});
            skLineSegment(sketch, "E496", {"start": v(53.8, 26.8) * mm, "end": v(53.93, 26.87) * mm});
            skLineSegment(sketch, "E497", {"start": v(53.93, 26.87) * mm, "end": v(54.06, 26.94) * mm});
            skLineSegment(sketch, "E498", {"start": v(54.06, 26.94) * mm, "end": v(54.39, 27.31) * mm});
            skLineSegment(sketch, "E499", {"start": v(54.39, 27.31) * mm, "end": v(54.37, 27.8) * mm});
            skLineSegment(sketch, "E500", {"start": v(54.37, 27.8) * mm, "end": v(54.1, 28.32) * mm});
            skLineSegment(sketch, "E501", {"start": v(54.1, 28.32) * mm, "end": v(53.85, 28.7) * mm});
            skLineSegment(sketch, "E502", {"start": v(53.85, 28.7) * mm, "end": v(53.78, 28.84) * mm});
            skLineSegment(sketch, "E503", {"start": v(53.78, 28.84) * mm, "end": v(53.86, 28.86) * mm});
            skLineSegment(sketch, "E504", {"start": v(53.86, 28.86) * mm, "end": v(54.13, 28.78) * mm});
            skLineSegment(sketch, "E505", {"start": v(54.13, 28.78) * mm, "end": v(54.58, 28.55) * mm});
            skLineSegment(sketch, "E506", {"start": v(54.58, 28.55) * mm, "end": v(55.01, 28.26) * mm});
            skLineSegment(sketch, "E507", {"start": v(55.01, 28.26) * mm, "end": v(55.27, 28.08) * mm});
            skLineSegment(sketch, "E508", {"start": v(55.27, 28.08) * mm, "end": v(55.35, 28.02) * mm});
            skLineSegment(sketch, "E509", {"start": v(55.35, 28.02) * mm, "end": v(55.5, 27.9) * mm});
            skLineSegment(sketch, "E510", {"start": v(55.5, 27.9) * mm, "end": v(56.22, 27.31) * mm});
            skLineSegment(sketch, "E511", {"start": v(56.22, 27.31) * mm, "end": v(56.95, 26.74) * mm});
            skLineSegment(sketch, "E512", {"start": v(56.95, 26.74) * mm, "end": v(57.1, 26.64) * mm});
            skLineSegment(sketch, "E513", {"start": v(57.1, 26.64) * mm, "end": v(57.25, 26.54) * mm});
            skLineSegment(sketch, "E514", {"start": v(57.25, 26.54) * mm, "end": v(57.98, 26.17) * mm});
            skLineSegment(sketch, "E515", {"start": v(57.98, 26.17) * mm, "end": v(58.77, 26) * mm});
            skLineSegment(sketch, "E516", {"start": v(58.77, 26) * mm, "end": v(58.94, 26.02) * mm});
            skLineSegment(sketch, "E517", {"start": v(58.94, 26.02) * mm, "end": v(59.05, 26.03) * mm});
            skLineSegment(sketch, "E518", {"start": v(59.05, 26.03) * mm, "end": v(59.36, 26.22) * mm});
            skLineSegment(sketch, "E519", {"start": v(59.36, 26.22) * mm, "end": v(59.43, 26.63) * mm});
            skLineSegment(sketch, "E520", {"start": v(59.43, 26.63) * mm, "end": v(59.32, 27.11) * mm});
            skLineSegment(sketch, "E521", {"start": v(59.32, 27.11) * mm, "end": v(59.25, 27.43) * mm});
            skLineSegment(sketch, "E522", {"start": v(59.25, 27.43) * mm, "end": v(59.25, 27.53) * mm});
            skLineSegment(sketch, "E523", {"start": v(59.25, 27.53) * mm, "end": v(59.37, 27.51) * mm});
            skLineSegment(sketch, "E524", {"start": v(59.37, 27.51) * mm, "end": v(59.71, 27.33) * mm});
            skLineSegment(sketch, "E525", {"start": v(59.71, 27.33) * mm, "end": v(60.2, 26.98) * mm});
            skLineSegment(sketch, "E526", {"start": v(60.2, 26.98) * mm, "end": v(60.65, 26.57) * mm});
            skLineSegment(sketch, "E527", {"start": v(60.65, 26.57) * mm, "end": v(60.95, 26.31) * mm});
            skLineSegment(sketch, "E528", {"start": v(60.95, 26.31) * mm, "end": v(61.06, 26.23) * mm});
            skLineSegment(sketch, "E529", {"start": v(61.06, 26.23) * mm, "end": v(61.2, 26.13) * mm});
            skLineSegment(sketch, "E530", {"start": v(61.2, 26.13) * mm, "end": v(61.84, 25.57) * mm});
            skLineSegment(sketch, "E531", {"start": v(61.84, 25.57) * mm, "end": v(62.41, 24.94) * mm});
            skLineSegment(sketch, "E532", {"start": v(62.41, 24.94) * mm, "end": v(62.51, 24.8) * mm});
            skLineSegment(sketch, "E533", {"start": v(62.51, 24.8) * mm, "end": v(62.72, 24.5) * mm});
            skLineSegment(sketch, "E534", {"start": v(62.72, 24.5) * mm, "end": v(63.76, 22.97) * mm});
            skLineSegment(sketch, "E535", {"start": v(63.76, 22.97) * mm, "end": v(64.87, 21.5) * mm});
            skLineSegment(sketch, "E536", {"start": v(64.87, 21.5) * mm, "end": v(65.12, 21.23) * mm});
            skLineSegment(sketch, "E537", {"start": v(65.12, 21.23) * mm, "end": v(65.39, 20.95) * mm});
            skLineSegment(sketch, "E538", {"start": v(65.39, 20.95) * mm, "end": v(66.87, 19.87) * mm});
            skLineSegment(sketch, "E539", {"start": v(66.87, 19.87) * mm, "end": v(68.57, 19.2) * mm});
            skLineSegment(sketch, "E540", {"start": v(68.57, 19.2) * mm, "end": v(68.95, 19.13) * mm});
            skLineSegment(sketch, "E541", {"start": v(68.95, 19.13) * mm, "end": v(69.03, 19.1) * mm});
            skLineSegment(sketch, "E542", {"start": v(69.03, 19.1) * mm, "end": v(69.3, 19.1) * mm});
            skLineSegment(sketch, "E543", {"start": v(69.3, 19.1) * mm, "end": v(69.88, 19.08) * mm});
            skLineSegment(sketch, "E544", {"start": v(69.88, 19.08) * mm, "end": v(70.57, 19.05) * mm});
            skLineSegment(sketch, "E545", {"start": v(70.57, 19.05) * mm, "end": v(71.3, 19) * mm});
            skLineSegment(sketch, "E546", {"start": v(71.3, 19) * mm, "end": v(71.97, 18.9) * mm});
            skLineSegment(sketch, "E547", {"start": v(71.97, 18.9) * mm, "end": v(72.5, 18.74) * mm});
            skLineSegment(sketch, "E548", {"start": v(72.5, 18.74) * mm, "end": v(72.8, 18.47) * mm});
            skLineSegment(sketch, "E549", {"start": v(72.8, 18.47) * mm, "end": v(72.83, 18.18) * mm});
            skLineSegment(sketch, "E550", {"start": v(72.83, 18.18) * mm, "end": v(72.8, 18.1) * mm});
            skLineSegment(sketch, "E551", {"start": v(72.8, 18.1) * mm, "end": v(72.74, 18) * mm});
            skLineSegment(sketch, "E552", {"start": v(72.74, 18) * mm, "end": v(72.66, 17.63) * mm});
            skLineSegment(sketch, "E553", {"start": v(72.66, 17.63) * mm, "end": v(72.73, 17.29) * mm});
            skLineSegment(sketch, "E554", {"start": v(72.73, 17.29) * mm, "end": v(72.9, 16.97) * mm});
            skLineSegment(sketch, "E555", {"start": v(72.9, 16.97) * mm, "end": v(73.02, 16.67) * mm});
            skLineSegment(sketch, "E556", {"start": v(73.02, 16.67) * mm, "end": v(73.05, 16.57) * mm});
            skLineSegment(sketch, "E557", {"start": v(73.05, 16.57) * mm, "end": v(73.08, 16.47) * mm});
            skLineSegment(sketch, "E558", {"start": v(73.08, 16.47) * mm, "end": v(73.07, 16.13) * mm});
            skLineSegment(sketch, "E559", {"start": v(73.07, 16.13) * mm, "end": v(72.98, 15.67) * mm});
            skLineSegment(sketch, "E560", {"start": v(72.98, 15.67) * mm, "end": v(72.91, 15.21) * mm});
            skLineSegment(sketch, "E561", {"start": v(72.91, 15.21) * mm, "end": v(72.93, 14.87) * mm});
            skLineSegment(sketch, "E562", {"start": v(72.93, 14.87) * mm, "end": v(72.97, 14.76) * mm});
            skLineSegment(sketch, "E563", {"start": v(72.97, 14.76) * mm, "end": v(73, 14.67) * mm});
            skLineSegment(sketch, "E564", {"start": v(73, 14.67) * mm, "end": v(73.06, 14.37) * mm});
            skLineSegment(sketch, "E565", {"start": v(73.06, 14.37) * mm, "end": v(73.04, 13.94) * mm});
            skLineSegment(sketch, "E566", {"start": v(73.04, 13.94) * mm, "end": v(72.9, 13.53) * mm});
            skLineSegment(sketch, "E567", {"start": v(72.9, 13.53) * mm, "end": v(72.7, 13.28) * mm});
            skLineSegment(sketch, "E568", {"start": v(72.7, 13.28) * mm, "end": v(72.62, 13.21) * mm});
            skLineSegment(sketch, "E569", {"start": v(72.62, 13.21) * mm, "end": v(72.52, 13.14) * mm});
            skLineSegment(sketch, "E570", {"start": v(72.52, 13.14) * mm, "end": v(72.16, 13.03) * mm});
            skLineSegment(sketch, "E571", {"start": v(72.16, 13.03) * mm, "end": v(71.7, 13.09) * mm});
            skLineSegment(sketch, "E572", {"start": v(71.7, 13.09) * mm, "end": v(71.25, 13.26) * mm});
            skLineSegment(sketch, "E573", {"start": v(71.25, 13.26) * mm, "end": v(70.93, 13.4) * mm});
            skLineSegment(sketch, "E574", {"start": v(70.93, 13.4) * mm, "end": v(70.82, 13.44) * mm});
            skLineSegment(sketch, "E575", {"start": v(70.82, 13.44) * mm, "end": v(70.53, 13.55) * mm});
            skLineSegment(sketch, "E576", {"start": v(70.53, 13.55) * mm, "end": v(69.01, 13.88) * mm});
            skLineSegment(sketch, "E577", {"start": v(69.01, 13.88) * mm, "end": v(67.48, 14.15) * mm});
            skLineSegment(sketch, "E578", {"start": v(67.48, 14.15) * mm, "end": v(67.18, 14.23) * mm});
            skLineSegment(sketch, "E579", {"start": v(67.18, 14.23) * mm, "end": v(67.02, 14.27) * mm});
            skLineSegment(sketch, "E580", {"start": v(67.02, 14.27) * mm, "end": v(65.48, 14.83) * mm});
            skLineSegment(sketch, "E581", {"start": v(65.48, 14.83) * mm, "end": v(65.32, 14.9) * mm});
            skLineSegment(sketch, "E582", {"start": v(65.32, 14.9) * mm, "end": v(65.18, 14.95) * mm});
            skLineSegment(sketch, "E583", {"start": v(65.18, 14.95) * mm, "end": v(64.5, 15.36) * mm});
            skLineSegment(sketch, "E584", {"start": v(64.5, 15.36) * mm, "end": v(63.8, 15.73) * mm});
            skLineSegment(sketch, "E585", {"start": v(63.8, 15.73) * mm, "end": v(63.65, 15.77) * mm});
            skLineSegment(sketch, "E586", {"start": v(63.65, 15.77) * mm, "end": v(63.49, 15.82) * mm});
            skLineSegment(sketch, "E587", {"start": v(63.49, 15.82) * mm, "end": v(62.73, 15.9) * mm});
            skLineSegment(sketch, "E588", {"start": v(62.73, 15.9) * mm, "end": v(61.98, 15.82) * mm});
            skLineSegment(sketch, "E589", {"start": v(61.98, 15.82) * mm, "end": v(61.81, 15.78) * mm});
            skLineSegment(sketch, "E590", {"start": v(61.81, 15.78) * mm, "end": v(61.78, 15.77) * mm});
            skLineSegment(sketch, "E591", {"start": v(61.78, 15.77) * mm, "end": v(61.7, 15.73) * mm});
            skLineSegment(sketch, "E592", {"start": v(61.7, 15.73) * mm, "end": v(61.48, 15.63) * mm});
            skLineSegment(sketch, "E593", {"start": v(61.48, 15.63) * mm, "end": v(61.22, 15.5) * mm});
            skLineSegment(sketch, "E594", {"start": v(61.22, 15.5) * mm, "end": v(60.95, 15.34) * mm});
            skLineSegment(sketch, "E595", {"start": v(60.95, 15.34) * mm, "end": v(60.71, 15.19) * mm});
            skLineSegment(sketch, "E596", {"start": v(60.71, 15.19) * mm, "end": v(60.55, 15.05) * mm});
            skLineSegment(sketch, "E597", {"start": v(60.55, 15.05) * mm, "end": v(60.5, 14.94) * mm});
            skLineSegment(sketch, "E598", {"start": v(60.5, 14.94) * mm, "end": v(60.6, 14.88) * mm});
            skLineSegment(sketch, "E599", {"start": v(60.6, 14.88) * mm, "end": v(60.62, 14.88) * mm});
            skLineSegment(sketch, "E600", {"start": v(60.62, 14.88) * mm, "end": v(60.76, 14.86) * mm});
            skLineSegment(sketch, "E601", {"start": v(60.76, 14.86) * mm, "end": v(61.4, 14.62) * mm});
            skLineSegment(sketch, "E602", {"start": v(61.4, 14.62) * mm, "end": v(62.03, 14.31) * mm});
            skLineSegment(sketch, "E603", {"start": v(62.03, 14.31) * mm, "end": v(62.15, 14.26) * mm});
            skLineSegment(sketch, "E604", {"start": v(62.15, 14.26) * mm, "end": v(62.26, 14.2) * mm});
            skLineSegment(sketch, "E605", {"start": v(62.26, 14.2) * mm, "end": v(62.56, 14.02) * mm});
            skLineSegment(sketch, "E606", {"start": v(62.56, 14.02) * mm, "end": v(63.03, 13.73) * mm});
            skLineSegment(sketch, "E607", {"start": v(63.03, 13.73) * mm, "end": v(63.5, 13.46) * mm});
            skLineSegment(sketch, "E608", {"start": v(63.5, 13.46) * mm, "end": v(63.8, 13.34) * mm});
            skLineSegment(sketch, "E609", {"start": v(63.8, 13.34) * mm, "end": v(63.9, 13.32) * mm});
            skLineSegment(sketch, "E610", {"start": v(63.9, 13.32) * mm, "end": v(64.55, 13.23) * mm});
            skLineSegment(sketch, "E611", {"start": v(64.55, 13.23) * mm, "end": v(67.7, 12.43) * mm});
            skLineSegment(sketch, "E612", {"start": v(67.7, 12.43) * mm, "end": v(70.8, 11.4) * mm});
            skLineSegment(sketch, "E613", {"start": v(70.8, 11.4) * mm, "end": v(71.42, 11.2) * mm});
            skLineSegment(sketch, "E614", {"start": v(71.42, 11.2) * mm, "end": v(71.55, 11.16) * mm});
            skLineSegment(sketch, "E615", {"start": v(71.55, 11.16) * mm, "end": v(72.15, 10.84) * mm});
            skLineSegment(sketch, "E616", {"start": v(72.15, 10.84) * mm, "end": v(72.72, 10.6) * mm});
            skLineSegment(sketch, "E617", {"start": v(72.72, 10.6) * mm, "end": v(72.9, 10.6) * mm});
            skLineSegment(sketch, "E618", {"start": v(72.9, 10.6) * mm, "end": v(73.05, 10.6) * mm});
            skLineSegment(sketch, "E619", {"start": v(73.05, 10.6) * mm, "end": v(73.49, 10.68) * mm});
            skLineSegment(sketch, "E620", {"start": v(73.49, 10.68) * mm, "end": v(73.75, 10.91) * mm});
            skLineSegment(sketch, "E621", {"start": v(73.75, 10.91) * mm, "end": v(73.82, 11.33) * mm});
            skLineSegment(sketch, "E622", {"start": v(73.82, 11.33) * mm, "end": v(73.83, 11.79) * mm});
            skLineSegment(sketch, "E623", {"start": v(73.83, 11.79) * mm, "end": v(73.83, 11.94) * mm});
            skLineSegment(sketch, "E624", {"start": v(73.83, 11.94) * mm, "end": v(74.04, 11.85) * mm});
            skLineSegment(sketch, "E625", {"start": v(74.04, 11.85) * mm, "end": v(74.6, 11.4) * mm});
            skLineSegment(sketch, "E626", {"start": v(74.6, 11.4) * mm, "end": v(75.34, 10.62) * mm});
            skLineSegment(sketch, "E627", {"start": v(75.34, 10.62) * mm, "end": v(76.03, 9.77) * mm});
            skLineSegment(sketch, "E628", {"start": v(76.03, 9.77) * mm, "end": v(76.5, 9.2) * mm});
            skLineSegment(sketch, "E629", {"start": v(76.5, 9.2) * mm, "end": v(76.66, 9.03) * mm});
            skLineSegment(sketch, "E630", {"start": v(76.66, 9.03) * mm, "end": v(76.77, 8.92) * mm});
            skLineSegment(sketch, "E631", {"start": v(76.77, 8.92) * mm, "end": v(77.5, 8.47) * mm});
            skLineSegment(sketch, "E632", {"start": v(77.5, 8.47) * mm, "end": v(78.3, 8.16) * mm});
            skLineSegment(sketch, "E633", {"start": v(78.3, 8.16) * mm, "end": v(78.45, 8.11) * mm});
            skLineSegment(sketch, "E634", {"start": v(78.45, 8.11) * mm, "end": v(78.59, 8.07) * mm});
            skLineSegment(sketch, "E635", {"start": v(78.59, 8.07) * mm, "end": v(79.02, 8.06) * mm});
            skLineSegment(sketch, "E636", {"start": v(79.02, 8.06) * mm, "end": v(79.27, 8.32) * mm});
            skLineSegment(sketch, "E637", {"start": v(79.27, 8.32) * mm, "end": v(79.33, 8.77) * mm});
            skLineSegment(sketch, "E638", {"start": v(79.33, 8.77) * mm, "end": v(79.34, 9.15) * mm});
            skLineSegment(sketch, "E639", {"start": v(79.34, 9.15) * mm, "end": v(79.36, 9.28) * mm});
            skLineSegment(sketch, "E640", {"start": v(79.36, 9.28) * mm, "end": v(79.36, 9.33) * mm});
            skLineSegment(sketch, "E641", {"start": v(79.36, 9.33) * mm, "end": v(79.42, 9.48) * mm});
            skLineSegment(sketch, "E642", {"start": v(79.42, 9.48) * mm, "end": v(79.53, 9.53) * mm});
            skLineSegment(sketch, "E643", {"start": v(79.53, 9.53) * mm, "end": v(79.68, 9.45) * mm});
            skLineSegment(sketch, "E644", {"start": v(79.68, 9.45) * mm, "end": v(79.84, 9.3) * mm});
            skLineSegment(sketch, "E645", {"start": v(79.84, 9.3) * mm, "end": v(80, 9.08) * mm});
            skLineSegment(sketch, "E646", {"start": v(80, 9.08) * mm, "end": v(80.15, 8.85) * mm});
            skLineSegment(sketch, "E647", {"start": v(80.15, 8.85) * mm, "end": v(80.27, 8.65) * mm});
            skLineSegment(sketch, "E648", {"start": v(80.27, 8.65) * mm, "end": v(80.32, 8.53) * mm});
            skLineSegment(sketch, "E649", {"start": v(80.32, 8.53) * mm, "end": v(80.33, 8.5) * mm});
            skLineSegment(sketch, "E650", {"start": v(80.33, 8.5) * mm, "end": v(80.39, 8.32) * mm});
            skLineSegment(sketch, "E651", {"start": v(80.39, 8.32) * mm, "end": v(80.7, 7.57) * mm});
            skLineSegment(sketch, "E652", {"start": v(80.7, 7.57) * mm, "end": v(81.13, 6.86) * mm});
            skLineSegment(sketch, "E653", {"start": v(81.13, 6.86) * mm, "end": v(81.24, 6.72) * mm});
            skLineSegment(sketch, "E654", {"start": v(81.24, 6.72) * mm, "end": v(81.4, 6.5) * mm});
            skLineSegment(sketch, "E655", {"start": v(81.4, 6.5) * mm, "end": v(81.94, 5.93) * mm});
            skLineSegment(sketch, "E656", {"start": v(81.94, 5.93) * mm, "end": v(82.74, 5.25) * mm});
            skLineSegment(sketch, "E657", {"start": v(82.74, 5.25) * mm, "end": v(83.6, 4.63) * mm});
            skLineSegment(sketch, "E658", {"start": v(83.6, 4.63) * mm, "end": v(84.26, 4.2) * mm});
            skLineSegment(sketch, "E659", {"start": v(84.26, 4.2) * mm, "end": v(84.48, 4.04) * mm});
            skLineSegment(sketch, "E660", {"start": v(84.48, 4.04) * mm, "end": v(84.43, 4.05) * mm});
            skLineSegment(sketch, "E661", {"start": v(84.43, 4.05) * mm, "end": v(84.27, 4.08) * mm});
            skLineSegment(sketch, "E662", {"start": v(84.27, 4.08) * mm, "end": v(84.03, 4.13) * mm});
            skLineSegment(sketch, "E663", {"start": v(84.03, 4.13) * mm, "end": v(83.75, 4.19) * mm});
            skLineSegment(sketch, "E664", {"start": v(83.75, 4.19) * mm, "end": v(83.49, 4.22) * mm});
            skLineSegment(sketch, "E665", {"start": v(83.49, 4.22) * mm, "end": v(83.24, 4.2) * mm});
            skLineSegment(sketch, "E666", {"start": v(83.24, 4.2) * mm, "end": v(83.04, 4.1) * mm});
            skLineSegment(sketch, "E667", {"start": v(83.04, 4.1) * mm, "end": v(82.92, 3.92) * mm});
            skLineSegment(sketch, "E668", {"start": v(82.92, 3.92) * mm, "end": v(82.88, 3.68) * mm});
            skLineSegment(sketch, "E669", {"start": v(82.88, 3.68) * mm, "end": v(82.89, 3.6) * mm});
            skLineSegment(sketch, "E670", {"start": v(82.89, 3.6) * mm, "end": v(82.9, 3.5) * mm});
            skLineSegment(sketch, "E671", {"start": v(82.9, 3.5) * mm, "end": v(83.1, 3.17) * mm});
            skLineSegment(sketch, "E672", {"start": v(83.1, 3.17) * mm, "end": v(83.54, 2.78) * mm});
            skLineSegment(sketch, "E673", {"start": v(83.54, 2.78) * mm, "end": v(84.05, 2.46) * mm});
            skLineSegment(sketch, "E674", {"start": v(84.05, 2.46) * mm, "end": v(84.38, 2.28) * mm});
            skLineSegment(sketch, "E675", {"start": v(84.38, 2.28) * mm, "end": v(84.48, 2.22) * mm});
            skLineSegment(sketch, "E676", {"start": v(84.48, 2.22) * mm, "end": v(84.7, 2.1) * mm});
            skLineSegment(sketch, "E677", {"start": v(84.7, 2.1) * mm, "end": v(85.48, 1.87) * mm});
            skLineSegment(sketch, "E678", {"start": v(85.48, 1.87) * mm, "end": v(86.6, 1.76) * mm});
            skLineSegment(sketch, "E679", {"start": v(86.6, 1.76) * mm, "end": v(87.75, 1.77) * mm});
            skLineSegment(sketch, "E680", {"start": v(87.75, 1.77) * mm, "end": v(88.55, 1.8) * mm});
            skLineSegment(sketch, "E681", {"start": v(88.55, 1.8) * mm, "end": v(88.82, 1.79) * mm});
            skLineSegment(sketch, "E682", {"start": v(88.82, 1.79) * mm, "end": v(88.7, 1.65) * mm});
            skLineSegment(sketch, "E683", {"start": v(88.7, 1.65) * mm, "end": v(88.24, 1.34) * mm});
            skLineSegment(sketch, "E684", {"start": v(88.24, 1.34) * mm, "end": v(87.34, 0.88) * mm});
            skLineSegment(sketch, "E685", {"start": v(87.34, 0.88) * mm, "end": v(86.4, 0.51) * mm});
            skLineSegment(sketch, "E686", {"start": v(86.4, 0.51) * mm, "end": v(85.86, 0.37) * mm});
            skLineSegment(sketch, "E687", {"start": v(85.86, 0.37) * mm, "end": v(85.68, 0.37) * mm});
            skLineSegment(sketch, "E688", {"start": v(85.68, 0.37) * mm, "end": v(85.44, 0.37) * mm});
            skLineSegment(sketch, "E689", {"start": v(85.44, 0.37) * mm, "end": v(84.73, 0.38) * mm});
            skLineSegment(sketch, "E690", {"start": v(84.73, 0.38) * mm, "end": v(83.84, 0.45) * mm});
            skLineSegment(sketch, "E691", {"start": v(83.84, 0.45) * mm, "end": v(82.98, 0.65) * mm});
            skLineSegment(sketch, "E692", {"start": v(82.98, 0.65) * mm, "end": v(82.31, 0.92) * mm});
            skLineSegment(sketch, "E693", {"start": v(82.31, 0.92) * mm, "end": v(82.1, 1.03) * mm});
            skLineSegment(sketch, "E694", {"start": v(82.1, 1.03) * mm, "end": v(81.86, 1.17) * mm});
            skLineSegment(sketch, "E695", {"start": v(81.86, 1.17) * mm, "end": v(80.69, 2.05) * mm});
            skLineSegment(sketch, "E696", {"start": v(80.69, 2.05) * mm, "end": v(79.7, 3.11) * mm});
            skLineSegment(sketch, "E697", {"start": v(79.7, 3.11) * mm, "end": v(79.54, 3.35) * mm});
            skLineSegment(sketch, "E698", {"start": v(79.54, 3.35) * mm, "end": v(79.4, 3.56) * mm});
            skLineSegment(sketch, "E699", {"start": v(79.4, 3.56) * mm, "end": v(78.96, 4.16) * mm});
            skLineSegment(sketch, "E700", {"start": v(78.96, 4.16) * mm, "end": v(78.34, 4.86) * mm});
            skLineSegment(sketch, "E701", {"start": v(78.34, 4.86) * mm, "end": v(77.66, 5.5) * mm});
            skLineSegment(sketch, "E702", {"start": v(77.66, 5.5) * mm, "end": v(77.07, 5.96) * mm});
            skLineSegment(sketch, "E703", {"start": v(77.07, 5.96) * mm, "end": v(76.87, 6.1) * mm});
            skLineSegment(sketch, "E704", {"start": v(76.87, 6.1) * mm, "end": v(76.87, 5.98) * mm});
            skLineSegment(sketch, "E705", {"start": v(76.87, 5.98) * mm, "end": v(76.78, 5.65) * mm});
            skLineSegment(sketch, "E706", {"start": v(76.78, 5.65) * mm, "end": v(76.56, 5.24) * mm});
            skLineSegment(sketch, "E707", {"start": v(76.56, 5.24) * mm, "end": v(76.23, 4.9) * mm});
            skLineSegment(sketch, "E708", {"start": v(76.23, 4.9) * mm, "end": v(75.93, 4.73) * mm});
            skLineSegment(sketch, "E709", {"start": v(75.93, 4.73) * mm, "end": v(75.83, 4.7) * mm});
            skLineSegment(sketch, "E710", {"start": v(75.83, 4.7) * mm, "end": v(75.77, 4.7) * mm});
            skLineSegment(sketch, "E711", {"start": v(75.77, 4.7) * mm, "end": v(75.6, 4.67) * mm});
            skLineSegment(sketch, "E712", {"start": v(75.6, 4.67) * mm, "end": v(75.31, 4.67) * mm});
            skLineSegment(sketch, "E713", {"start": v(75.31, 4.67) * mm, "end": v(75, 4.69) * mm});
            skLineSegment(sketch, "E714", {"start": v(75, 4.69) * mm, "end": v(74.7, 4.75) * mm});
            skLineSegment(sketch, "E715", {"start": v(74.7, 4.75) * mm, "end": v(74.44, 4.85) * mm});
            skLineSegment(sketch, "E716", {"start": v(74.44, 4.85) * mm, "end": v(74.27, 5) * mm});
            skLineSegment(sketch, "E717", {"start": v(74.27, 5) * mm, "end": v(74.23, 5.19) * mm});
            skLineSegment(sketch, "E718", {"start": v(74.23, 5.19) * mm, "end": v(74.3, 5.39) * mm});
            skLineSegment(sketch, "E719", {"start": v(74.3, 5.39) * mm, "end": v(74.35, 5.44) * mm});
            skLineSegment(sketch, "E720", {"start": v(74.35, 5.44) * mm, "end": v(74.44, 5.55) * mm});
            skLineSegment(sketch, "E721", {"start": v(74.44, 5.55) * mm, "end": v(74.6, 5.94) * mm});
            skLineSegment(sketch, "E722", {"start": v(74.6, 5.94) * mm, "end": v(74.61, 6.43) * mm});
            skLineSegment(sketch, "E723", {"start": v(74.61, 6.43) * mm, "end": v(74.43, 6.9) * mm});
            skLineSegment(sketch, "E724", {"start": v(74.43, 6.9) * mm, "end": v(74.1, 7.35) * mm});
            skLineSegment(sketch, "E725", {"start": v(74.1, 7.35) * mm, "end": v(73.68, 7.77) * mm});
            skLineSegment(sketch, "E726", {"start": v(73.68, 7.77) * mm, "end": v(73.21, 8.15) * mm});
            skLineSegment(sketch, "E727", {"start": v(73.21, 8.15) * mm, "end": v(72.76, 8.5) * mm});
            skLineSegment(sketch, "E728", {"start": v(72.76, 8.5) * mm, "end": v(72.46, 8.71) * mm});
            skLineSegment(sketch, "E729", {"start": v(72.46, 8.71) * mm, "end": v(72.36, 8.79) * mm});
            skLineSegment(sketch, "E730", {"start": v(72.36, 8.79) * mm, "end": v(72.14, 8.95) * mm});
            skLineSegment(sketch, "E731", {"start": v(60.7, 21.86) * mm, "end": v(60.63, 21.94) * mm});
            skLineSegment(sketch, "E732", {"start": v(60.63, 21.94) * mm, "end": v(60.4, 22.13) * mm});
            skLineSegment(sketch, "E733", {"start": v(60.4, 22.13) * mm, "end": v(59.91, 22.46) * mm});
            skLineSegment(sketch, "E734", {"start": v(59.91, 22.46) * mm, "end": v(59.3, 22.82) * mm});
            skLineSegment(sketch, "E735", {"start": v(59.3, 22.82) * mm, "end": v(58.63, 23.14) * mm});
            skLineSegment(sketch, "E736", {"start": v(58.63, 23.14) * mm, "end": v(57.96, 23.38) * mm});
            skLineSegment(sketch, "E737", {"start": v(57.96, 23.38) * mm, "end": v(57.37, 23.46) * mm});
            skLineSegment(sketch, "E738", {"start": v(57.37, 23.46) * mm, "end": v(56.93, 23.34) * mm});
            skLineSegment(sketch, "E739", {"start": v(56.93, 23.34) * mm, "end": v(56.71, 23.07) * mm});
            skLineSegment(sketch, "E740", {"start": v(56.71, 23.07) * mm, "end": v(56.7, 22.96) * mm});
            skLineSegment(sketch, "E741", {"start": v(56.7, 22.96) * mm, "end": v(56.67, 22.85) * mm});
            skLineSegment(sketch, "E742", {"start": v(56.67, 22.85) * mm, "end": v(56.75, 22.48) * mm});
            skLineSegment(sketch, "E743", {"start": v(56.75, 22.48) * mm, "end": v(57.09, 22.12) * mm});
            skLineSegment(sketch, "E744", {"start": v(57.09, 22.12) * mm, "end": v(57.63, 21.86) * mm});
            skLineSegment(sketch, "E745", {"start": v(57.63, 21.86) * mm, "end": v(58.3, 21.7) * mm});
            skLineSegment(sketch, "E746", {"start": v(58.3, 21.7) * mm, "end": v(59.02, 21.64) * mm});
            skLineSegment(sketch, "E747", {"start": v(59.02, 21.64) * mm, "end": v(59.72, 21.65) * mm});
            skLineSegment(sketch, "E748", {"start": v(59.72, 21.65) * mm, "end": v(60.3, 21.73) * mm});
            skLineSegment(sketch, "E749", {"start": v(60.3, 21.73) * mm, "end": v(60.6, 21.81) * mm});
            skLineSegment(sketch, "E750", {"start": v(60.6, 21.81) * mm, "end": v(60.7, 21.86) * mm});
            skArc(sketch, "E751", {"start": v(72.14, 8.95) * mm, "mid": v(70.45, 9.55) * mm, "end": v(68.67, 9.41) * mm});
            skSolve(sketch);
        }
        {
            var Q0;
            Q0 = qSketchRegion(id + "F2", true);
            extrude(context, id + "F3", {"entities" : qUnion([Q0]), "operationType" : NewBodyOperationType.ADD, "depth" : 6.35 * mm, "offsetDistance" : 25.4 * mm});
        }
    });
